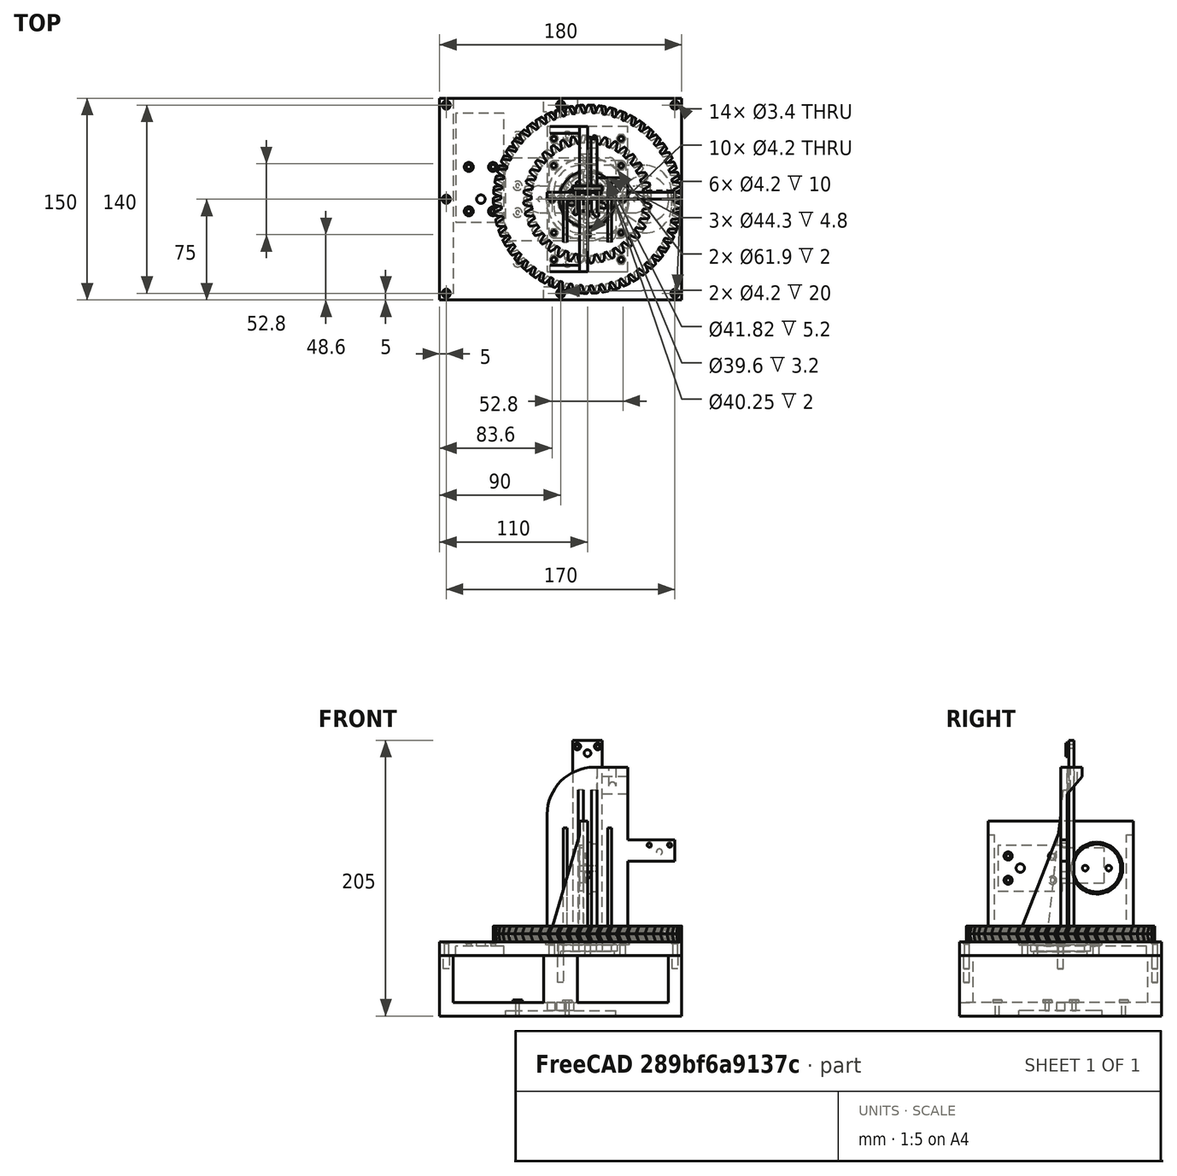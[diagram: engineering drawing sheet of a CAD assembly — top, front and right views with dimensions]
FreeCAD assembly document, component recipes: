
FREECAD ASSEMBLY — COMPONENT RECIPES ("antenna_tracker_alternative_gears_v0.6.5")

This assembly document has 24 components, labeled P0..P23 below (a component is one placed body or linked part). 18 of them carry a construction recipe — the FreeCAD feature program that regenerates the part from scratch, quoted from this document or its linked companion documents; the rest are supplied as boundary geometry only. No exploded tour is included for this assembly.
COMPONENT P0 — geometry summary ("GY_511_LSM303DLHC001"; no construction recipe available for this part):
  bounding box: 20.9 x 14.6 x 3.8 mm
  tessellated surface: 5,190 triangles
  volume: 500 mm^3 (43% of its bounding box)
COMPONENT P1 — geometry summary ("GY_511_LSM303DLHC002"; no construction recipe available for this part):
  bounding box: 20.9 x 14.6 x 3.8 mm
  tessellated surface: 5,190 triangles
  volume: 500 mm^3 (43% of its bounding box)
COMPONENT P2 — geometry summary ("GY_511_LSM303DLHC002"; no construction recipe available for this part):
  bounding box: 20.9 x 14.6 x 3.8 mm
  tessellated surface: 5,190 triangles
  volume: 500 mm^3 (43% of its bounding box)
COMPONENT P3 — geometry summary ("L298N v003"; no construction recipe available for this part):
  bounding box: 43.0 x 43.0 x 27.9 mm
  tessellated surface: 26,858 triangles
  volume: 10819 mm^3 (21% of its bounding box)
COMPONENT P4 — geometry summary ("ZWL-FP Motor_az"; no construction recipe available for this part):
  bounding box: 81.2 x 41.0 x 32.0 mm
  tessellated surface: 60,924 triangles
  volume: 36469 mm^3 (34% of its bounding box)
COMPONENT P5 — geometry summary ("ZWL-FP Motor_el"; no construction recipe available for this part):
  bounding box: 81.2 x 41.0 x 32.0 mm
  tessellated surface: 60,924 triangles
  volume: 36469 mm^3 (34% of its bounding box)
COMPONENT P6 — recipe-attached ("6707-2r_az", modeled in this document).
Construction recipe (the document's own serialized feature program — sketch geometry with constraints, then the solid features built on it; lengths are millimeters unless a unit is written):

FEATURE [Sketcher::SketchObject] Sketch002  label="bearing_outside"
  ArcFitTolerance = 1e-06
  AttachmentSupport = -> [XY_Plane004]
  ExternalTypes = [0]
  FullyConstrained = true
  MakeInternals = false
  MapMode = 5
  expr: Constraints[2] = VarSet.Base_bearing_outside_diameter
  expr: Constraints[3] = VarSet.Base_bearing_outside_diameter_inside
  sketch-geometry (2):
    g0: Circle CenterX=0 CenterY=0 CenterZ=0 NormalX=0 NormalY=0 NormalZ=1 AngleXU=0 Radius=22
    g1: Circle CenterX=0 CenterY=0 CenterZ=0 NormalX=0 NormalY=0 NormalZ=1 AngleXU=0 Radius=20.5
  constraints (4):
    c: Coincident(g0,g-1)
    c: Coincident(g1,g0)
    c: Diameter(g0) = 44
    c: Diameter(g1) = 41
FEATURE [PartDesign::Pad] Pad001
  Direction = (0,0,1)
  Length = 4.8
  Length2 = 10
  Profile = -> Sketch002
  ReferenceAxis = -> Sketch002 [N_Axis]
  Refine = true
  Suppressed = false
  Type = 0
  expr: Length = VarSet.Base_bearing_thickness
FEATURE [Sketcher::SketchObject] Sketch025  label="bearing_inside001"
  ArcFitTolerance = 1e-06
  AttachmentSupport = -> [XY_Plane004]
  ExternalTypes = [0]
  FullyConstrained = true
  MakeInternals = false
  MapMode = 5
  expr: Constraints[2] = VarSet.Base_bearing_inside_diameter_outside
  expr: Constraints[3] = VarSet.Base_bearing_inside_diameter
  sketch-geometry (5):
    g0: ArcOfCircle CenterX=0 CenterY=0 CenterZ=0 NormalX=0 NormalY=0 NormalZ=1 AngleXU=0 Radius=19 StartAngle=1.62345 EndAngle=7.80133
    g1: Circle CenterX=0 CenterY=0 CenterZ=0 NormalX=0 NormalY=0 NormalZ=1 AngleXU=0 Radius=17.5
    g2: LineSegment StartX=1 StartY=18.9737 StartZ=0 EndX=1 EndY=20.9737 EndZ=0
    g3: LineSegment StartX=-1 StartY=18.9737 StartZ=0 EndX=-1 EndY=20.9737 EndZ=0
    g4: LineSegment StartX=-1 StartY=20.9737 StartZ=0 EndX=1 EndY=20.9737 EndZ=0
  constraints (13):
    c: Coincident(g0,g-1)
    c: Coincident(g1,g0)
    c: Diameter(g0) = 38
    c: Diameter(g1) = 35
    c: Vertical(g2)
    c: Vertical(g3)
    c: Coincident(g4,g3)
    c: Coincident(g4,g2)
    c: Coincident(g0,g2)
    c: Coincident(g0,g3)
    c: DistanceX(g3,g2) = 2
    c: Symmetric(g3,g2,g-2)
    c: DistanceY(g0,g2) = 2
FEATURE [PartDesign::Pad] Pad024
  BaseFeature = -> Pad001
  Direction = (0,0,1)
  Length = 4.8
  Length2 = 10
  Profile = -> Sketch025
  ReferenceAxis = -> Sketch025 [N_Axis]
  Refine = true
  Suppressed = false
  Type = 0
  expr: Length = VarSet.Base_bearing_thickness
FEATURE [PartDesign::Body] Body002  label="6707-2r"
  AllowCompound = false
  Group = -> [Sketch002,Pad001,Sketch025,Pad024]
  Origin = -> Origin004
  Tip = -> Pad024
COMPONENT P7 — same part as P6; its construction recipe is shown at P6.
COMPONENT P8 — same part as P6; its construction recipe is shown at P6.
COMPONENT P9 — same part as P6; its construction recipe is shown at P6.
COMPONENT P10 — recipe-attached ("antenna_mount002", modeled in this document).
Construction recipe (the document's own serialized feature program — sketch geometry with constraints, then the solid features built on it; lengths are millimeters unless a unit is written):

FEATURE [Sketcher::SketchObject] Sketch031
  ArcFitTolerance = 1e-06
  AttachmentSupport = -> [XY_Plane022]
  ExternalTypes = [0]
  FullyConstrained = true
  MakeInternals = false
  MapMode = 5
  expr: Constraints[10] = VarSet.Base_antenna_base_x
  expr: Constraints[11] = VarSet.Base_antenna_base_y
  expr: Constraints[30] = VarSet.Base_antenna_base_x * 1.15
  expr: Constraints[31] = VarSet.Base_antenna_base_y * 1.15
  sketch-geometry (14):
    g0: LineSegment [constr] StartX=-25 StartY=25 StartZ=0 EndX=-25 EndY=-25 EndZ=0
    g1: LineSegment [constr] StartX=-25 StartY=-25 StartZ=0 EndX=25 EndY=-25 EndZ=0
    g2: LineSegment [constr] StartX=25 StartY=-25 StartZ=0 EndX=25 EndY=25 EndZ=0
    g3: LineSegment [constr] StartX=25 StartY=25 StartZ=0 EndX=-25 EndY=25 EndZ=0
    g4: GeomPoint [constr] X=0 Y=0 Z=0
    g5: Circle CenterX=-25 CenterY=25 CenterZ=0 NormalX=0 NormalY=0 NormalZ=1 AngleXU=0 Radius=1.55
    g6: Circle CenterX=25 CenterY=25 CenterZ=0 NormalX=0 NormalY=0 NormalZ=1 AngleXU=0 Radius=1.55
    g7: Circle CenterX=25 CenterY=-25 CenterZ=0 NormalX=0 NormalY=0 NormalZ=1 AngleXU=0 Radius=1.55
    g8: Circle CenterX=-25 CenterY=-25 CenterZ=0 NormalX=0 NormalY=0 NormalZ=1 AngleXU=0 Radius=1.55
    g9: LineSegment StartX=-28.75 StartY=28.75 StartZ=0 EndX=-28.75 EndY=-28.75 EndZ=0
    g10: LineSegment StartX=-28.75 StartY=-28.75 StartZ=0 EndX=28.75 EndY=-28.75 EndZ=0
    g11: LineSegment StartX=28.75 StartY=-28.75 StartZ=0 EndX=28.75 EndY=28.75 EndZ=0
    g12: LineSegment StartX=28.75 StartY=28.75 StartZ=0 EndX=-28.75 EndY=28.75 EndZ=0
    g13: GeomPoint [constr] X=0 Y=0 Z=0
  constraints (32):
    c: Coincident(g0,g1)
    c: Coincident(g1,g2)
    c: Coincident(g2,g3)
    c: Coincident(g3,g0)
    c: Vertical(g0)
    c: Vertical(g2)
    c: Horizontal(g1)
    c: Horizontal(g3)
    c: Symmetric(g2,g0,g4)
    c: Coincident(g4,g-1)
    c: DistanceX(g0,g2) = 50
    c: DistanceY(g0,g0) = 50
    c: Coincident(g5,g0)
    c: Coincident(g6,g2)
    c: Coincident(g7,g1)
    c: Coincident(g8,g0)
    c: Equal(g8,g7)
    c: Equal(g7,g6)
    c: Equal(g6,g5)
    c: Diameter(g5) = 3.1
    c: Coincident(g9,g10)
    c: Coincident(g10,g11)
    c: Coincident(g11,g12)
    c: Coincident(g12,g9)
    c: Vertical(g9)
    c: Vertical(g11)
    c: Horizontal(g10)
    c: Horizontal(g12)
    c: Symmetric(g11,g9,g13)
    c: Coincident(g13,g4)
    c: DistanceX(g12,g12) = 57.5
    c: DistanceY(g9,g9) = 57.5
FEATURE [PartDesign::Pad] Pad029
  Direction = (0,0,1)
  Length = 5
  Length2 = 10
  Profile = -> Sketch031
  ReferenceAxis = -> Sketch031 [N_Axis]
  Refine = true
  Suppressed = false
  Type = 0
FEATURE [Sketcher::SketchObject] Sketch059  label="vertical_base"
  ArcFitTolerance = 1e-06
  AttachmentSupport = -> [XY_Plane043]
  ExternalTypes = [0]
  FullyConstrained = true
  MakeInternals = false
  MapMode = 5
  sketch-geometry (4):
    g0: LineSegment StartX=-30 StartY=0 StartZ=0 EndX=30 EndY=0 EndZ=0
    g1: LineSegment StartX=30 StartY=0 StartZ=0 EndX=30 EndY=5 EndZ=0
    g2: LineSegment StartX=30 StartY=5 StartZ=0 EndX=-30 EndY=5 EndZ=0
    g3: LineSegment StartX=-30 StartY=5 StartZ=0 EndX=-30 EndY=0 EndZ=0
  constraints (11):
    c: Coincident(g0,g1)
    c: Coincident(g1,g2)
    c: Coincident(g2,g3)
    c: Coincident(g3,g0)
    c: Horizontal(g0)
    c: Vertical(g1)
    c: Vertical(g3)
    c: Distance(g1,g3) = 60
    c: Distance(g0,g2) = 5
    c: PointOnObject(g0,g-1)
    c: Symmetric(g2,g1,g-2)
FEATURE [PartDesign::Pad] Pad043
  Direction = (0,0,1)
  Length = 130
  Length2 = 10
  Profile = -> Sketch059
  ReferenceAxis = -> Sketch059 [N_Axis]
  Refine = true
  Suppressed = false
  Type = 0
FEATURE [Sketcher::SketchObject] Sketch060  label="trust"
  ArcFitTolerance = 1e-06
  AttachmentOffset = pos=(0,0,-18) rot=(0,0,1;0rad)
  AttachmentSupport = -> [YZ_Plane043]
  ExternalTypes = [0]
  FullyConstrained = true
  MakeInternals = false
  MapMode = 5
  Placement = pos=(-18,0,0) rot=(0.57735,0.57735,0.57735;2.0944rad)
  sketch-geometry (4):
    g0: LineSegment StartX=0 StartY=0 StartZ=0 EndX=0 EndY=85 EndZ=0
    g1: LineSegment StartX=-32 StartY=0 StartZ=0 EndX=0 EndY=0 EndZ=0
    g2: LineSegment StartX=-32 StartY=0 StartZ=0 EndX=-32 EndY=3 EndZ=0
    g3: LineSegment StartX=-32 StartY=3 StartZ=0 EndX=0 EndY=85 EndZ=0
  constraints (11):
    c: Coincident(g-1,g0)
    c: PointOnObject(g0,g-2)
    c: PointOnObject(g1,g-1)
    c: Coincident(g1,g0)
    c: DistanceY(g-1,g0) = 85
    c: DistanceX(g1,g0) = 32
    c: Coincident(g2,g3)
    c: Coincident(g3,g0)
    c: Parallel(g2,g0)
    c: Distance(g2,g2) = 3
    c: Coincident(g2,g1)
FEATURE [PartDesign::Pad] Pad044
  BaseFeature = -> Pad043
  Direction = (1,0,0)
  Length = 3
  Length2 = 10
  Profile = -> Sketch060
  ReferenceAxis = -> Sketch060 [N_Axis]
  Refine = true
  Suppressed = false
  Type = 0
FEATURE [PartDesign::Mirrored] Mirrored
  BaseFeature = -> Pad044
  MirrorPlane = -> YZ_Plane043
  Originals = -> [Pad044]
  Refine = true
  Suppressed = false
  TransformMode = 0
FEATURE [Sketcher::SketchObject] Sketch061  label="antenna_hole"
  ArcFitTolerance = 1e-06
  AttachmentSupport = -> [Mirrored]
  ExternalTypes = [0]
  FullyConstrained = true
  MakeInternals = false
  MapMode = 5
  Placement = pos=(0,5,0) rot=(0,0.707107,0.707107;3.14159rad)
  sketch-geometry (1):
    g0: Circle CenterX=0 CenterY=50 CenterZ=0 NormalX=0 NormalY=0 NormalZ=1 AngleXU=0 Radius=2.6
  constraints (3):
    c: PointOnObject(g0,g-2)
    c: DistanceY(g-1,g0) = 50
    c: Diameter(g0) = 5.2
FEATURE [Sketcher::SketchObject] Sketch062  label="vertical_mount_antenna"
  ArcFitTolerance = 1e-06
  ExternalTypes = [0]
  FullyConstrained = true
  MakeInternals = false
  MapMode = 5
  Placement = pos=(0,0,130) rot=(0,0,1;0rad)
  sketch-geometry (6):
    g0: LineSegment StartX=7 StartY=0 StartZ=0 EndX=30 EndY=0 EndZ=0
    g1: LineSegment StartX=30 StartY=0 StartZ=0 EndX=30 EndY=16 EndZ=0
    g2: LineSegment StartX=30 StartY=16 StartZ=0 EndX=7 EndY=16 EndZ=0
    g3: LineSegment StartX=7 StartY=16 StartZ=0 EndX=7 EndY=0 EndZ=0
    g4: Circle CenterX=18.5 CenterY=10 CenterZ=0 NormalX=0 NormalY=0 NormalZ=1 AngleXU=0 Radius=2.6
    g5: LineSegment [constr] StartX=18.5 StartY=0 StartZ=0 EndX=18.5 EndY=16 EndZ=0
  constraints (17):
    c: Coincident(g0,g1)
    c: Coincident(g1,g2)
    c: Coincident(g2,g3)
    c: Coincident(g3,g0)
    c: Horizontal(g2)
    c: Vertical(g1)
    c: Vertical(g3)
    c: Distance(g1,g3) = 23
    c: Distance(g0,g2) = 16
    c: PointOnObject(g0,g-1)
    c: Diameter(g4) = 5.2
    c: DistanceY(g-1,g4) = 10
    c: Symmetric(g0,g0,g5)
    c: Symmetric(g2,g2,g5)
    c: PointOnObject(g0,g-1)
    c: PointOnObject(g4,g5)
    c: DistanceX(g-1,g0) = 7
FEATURE [PartDesign::Pad] Pad045
  BaseFeature = -> Mirrored
  Direction = (0,0,1)
  Length = 20
  Length2 = 10
  Profile = -> Sketch062
  ReferenceAxis = -> Sketch062 [N_Axis]
  Refine = true
  Reversed = true
  Suppressed = false
  Type = 0
FEATURE [Sketcher::SketchObject] Sketch063
  ArcFitTolerance = 1e-06
  AttachmentSupport = -> [YZ_Plane043]
  ExternalGeometry = -> [Pad045]
  ExternalTypes = [0,0,0]
  FullyConstrained = true
  MakeInternals = false
  MapMode = 5
  Placement = pos=(0,0,0) rot=(0.57735,0.57735,0.57735;2.0944rad)
  sketch-geometry (3):
    g0: LineSegment StartX=16 StartY=110 StartZ=0 EndX=16 EndY=123 EndZ=0
    g1: LineSegment StartX=16 StartY=123 StartZ=0 EndX=5 EndY=110 EndZ=0
    g2: LineSegment StartX=5 StartY=110 StartZ=0 EndX=16 EndY=110 EndZ=0
  constraints (8):
    c: Coincident(g0,g1)
    c: PointOnObject(g0,g-4)
    c: Coincident(g2,g1)
    c: Coincident(g2,g0)
    c: Coincident(g0,g-4)
    c: Coincident(g1,g-5)
    c: Angle(g1,g0) = 0.702257
    c: DistanceY(g0,g-4) = 7
FEATURE [PartDesign::Pocket] Pocket041
  BaseFeature = -> Pad045
  Direction = (-1,0,0)
  Length = 5
  Length2 = 5
  Midplane = true
  Profile = -> Sketch063
  ReferenceAxis = -> Sketch063 [N_Axis]
  Refine = true
  Suppressed = false
  Type = 1
FEATURE [PartDesign::Fillet] Fillet001
  Base = -> Pad029 [Edge5,Edge8,Edge1,Edge2]
  BaseFeature = -> Pad029
  Radius = 4
  Refine = true
  SupportTransform = false
  Suppressed = false
  UseAllEdges = false
FEATURE [PartDesign::Body] Body011  label="antenna_mount_body"
  AllowCompound = false
  Group = -> [Sketch031,Pad029,Fillet001]
  Origin = -> Origin038
  Tip = -> Fillet001
FEATURE [Sketcher::SketchObject] Sketch067  label="sensor_mount"
  ArcFitTolerance = 1e-06
  AttachmentSupport = -> [XZ_Plane043]
  ExternalTypes = [0]
  FullyConstrained = true
  MakeInternals = false
  MapMode = 5
  Placement = pos=(0,0,0) rot=(1,0,0;1.5708rad)
  sketch-geometry (12):
    g0: LineSegment StartX=0 StartY=76 StartZ=0 EndX=0 EndY=60 EndZ=0
    g1: LineSegment StartX=0 StartY=60 StartZ=0 EndX=65 EndY=60 EndZ=0
    g2: LineSegment StartX=65 StartY=60 StartZ=0 EndX=65 EndY=76 EndZ=0
    g3: LineSegment StartX=65 StartY=76 StartZ=0 EndX=0 EndY=76 EndZ=0
    g4: LineSegment [constr] StartX=65 StartY=72 StartZ=0 EndX=0 EndY=72 EndZ=0
    g5: Circle CenterX=61 CenterY=72 CenterZ=0 NormalX=0 NormalY=0 NormalZ=1 AngleXU=0 Radius=1.4
    g6: Circle CenterX=45.9 CenterY=72 CenterZ=0 NormalX=0 NormalY=0 NormalZ=1 AngleXU=0 Radius=1.4
    g7: Circle CenterX=45.9 CenterY=72 CenterZ=0 NormalX=0 NormalY=0 NormalZ=1 AngleXU=0 Radius=2.2
    g8: Circle CenterX=61 CenterY=72 CenterZ=0 NormalX=0 NormalY=0 NormalZ=1 AngleXU=0 Radius=2.2
    g9: Circle CenterX=53.45 CenterY=67 CenterZ=0 NormalX=0 NormalY=0 NormalZ=1 AngleXU=0 Radius=2.2
    g10: GeomPoint X=53.45 Y=72 Z=0
    g11: LineSegment [constr] StartX=53.45 StartY=72 StartZ=0 EndX=53.45 EndY=67 EndZ=0
  constraints (32):
    c: Coincident(g0,g1)
    c: Coincident(g1,g2)
    c: Coincident(g2,g3)
    c: Coincident(g3,g0)
    c: Vertical(g0)
    c: Vertical(g2)
    c: Horizontal(g1)
    c: Horizontal(g3)
    c: PointOnObject(g0,g-2)
    c: DistanceY(g0,g0) = 16
    c: DistanceX(g0,g1) = 65
    c: DistanceY(g-1,g0) = 60
    c: PointOnObject(g4,g2)
    c: PointOnObject(g4,g0)
    c: Horizontal(g4)
    c: Distance(g4,g2) = 4
    c: PointOnObject(g5,g4)
    c: PointOnObject(g6,g4)
    c: Diameter(g6) = 2.8
    c: Coincident(g7,g6)
    c: Coincident(g8,g5)
    c: Equal(g6,g5)
    c: Diameter(g7) = 4.4
    c: Equal(g7,g8)
    c: DistanceX(g6,g5) = 15.1
    c: DistanceX(g5,g4) = 4
    c: Equal(g7,g9)
    c: Symmetric(g6,g5,g10)
    c: Coincident(g11,g10)
    c: Vertical(g11)
    c: Coincident(g9,g11)
    c: DistanceY(g9,g10) = 5
FEATURE [PartDesign::Pad] Pad048
  BaseFeature = -> Pocket041
  Direction = (0,-1,2e-16)
  Length = 5
  Length2 = 10
  Profile = -> Sketch067 [Edge2,Edge1,Edge4,Edge3]
  ReferenceAxis = -> Sketch067 [N_Axis]
  Refine = true
  Reversed = true
  Suppressed = false
  Type = 0
FEATURE [PartDesign::Pad] Pad049
  BaseFeature = -> Pad048
  Direction = (0,-1,2e-16)
  Length = 6
  Length2 = 10
  Profile = -> Sketch067 [Edge8,Edge9,Edge7]
  ReferenceAxis = -> Sketch067 [N_Axis]
  Refine = true
  Reversed = true
  Suppressed = false
  Type = 0
FEATURE [PartDesign::Pocket] Pocket044
  BaseFeature = -> Pad049
  Direction = (0,1,-2e-16)
  Length = 5
  Length2 = 5
  Midplane = true
  Profile = -> Sketch067 [Edge6,Edge5]
  ReferenceAxis = -> Sketch067 [N_Axis]
  Refine = true
  Suppressed = false
  Type = 1
FEATURE [PartDesign::Pocket] Pocket045
  BaseFeature = -> Pocket044
  Direction = (0,-1,2e-16)
  Length = 5
  Length2 = 5
  Midplane = true
  Profile = -> Sketch061
  ReferenceAxis = -> Sketch061 [N_Axis]
  Refine = true
  Suppressed = false
  Type = 1
FEATURE [PartDesign::Fillet] Fillet
  Base = -> Pocket045 [Edge30]
  BaseFeature = -> Pocket045
  Radius = 35
  Refine = true
  SupportTransform = false
  Suppressed = false
  UseAllEdges = false
FEATURE [PartDesign::Body] Body019  label="helix_yagi"
  AllowCompound = false
  Group = -> [Sketch059,Pad043,Sketch060,Pad044,Mirrored,Sketch061,Sketch062,Pad045,Sketch063,Pocket041,Sketch067,Pad048,Pad049,Pocket044,Pocket045,Fillet]
  Origin = -> Origin080
  Tip = -> Fillet
COMPONENT P11 — recipe-attached ("base003", modeled in this document).
Construction recipe (the document's own serialized feature program — sketch geometry with constraints, then the solid features built on it; lengths are millimeters unless a unit is written):

FEATURE [Sketcher::SketchObject] Sketch001  label="outside"
  ArcFitTolerance = 1e-06
  AttachmentSupport = -> [XY_Plane003]
  ExternalTypes = [0]
  FullyConstrained = true
  MakeInternals = false
  MapMode = 5
  expr: Constraints[8] = VarSet.Base_base_y
  expr: Constraints[9] = VarSet.Base_base_x
  sketch-geometry (5):
    g0: LineSegment StartX=-110 StartY=-75 StartZ=0 EndX=70 EndY=-75 EndZ=0
    g1: LineSegment StartX=70 StartY=-75 StartZ=0 EndX=70 EndY=75 EndZ=0
    g2: LineSegment StartX=70 StartY=75 StartZ=0 EndX=-110 EndY=75 EndZ=0
    g3: LineSegment StartX=-110 StartY=75 StartZ=0 EndX=-110 EndY=-75 EndZ=0
    g4: GeomPoint [constr] X=0 Y=0 Z=0
  constraints (12):
    c: Coincident(g0,g1)
    c: Coincident(g1,g2)
    c: Coincident(g2,g3)
    c: Coincident(g3,g0)
    c: Horizontal(g0)
    c: Horizontal(g2)
    c: Vertical(g1)
    c: Coincident(g4,g-1)
    c: DistanceY(g0,g2) = 150
    c: DistanceX(g2,g1) = 180
    c: DistanceX(g2,g-1) = 110
    c: Symmetric(g0,g2,g-1)
FEATURE [PartDesign::Pad] Pad
  Direction = (0,0,1)
  Length = 10
  Length2 = 10
  Profile = -> Sketch001
  ReferenceAxis = -> Sketch001 [N_Axis]
  Refine = true
  Reversed = true
  Suppressed = false
  Type = 0
  expr: Length = VarSet.Base_base_thickness
FEATURE [Sketcher::SketchObject] Sketch  label="motor"
  ArcFitTolerance = 1e-06
  AttachmentSupport = -> [XY_Plane003]
  ExternalTypes = [0]
  FullyConstrained = true
  MakeInternals = false
  MapMode = 5
  expr: Constraints[0] = 6 mm + VarSet.Base_tolerance_inside_circle
  expr: Constraints[2] = VarSet.Base_distance_grat_az
  sketch-geometry (10):
    g0: Circle CenterX=-79.3 CenterY=0 CenterZ=0 NormalX=0 NormalY=0 NormalZ=1 AngleXU=0 Radius=3.15
    g1: LineSegment [constr] StartX=-88.3 StartY=-9 StartZ=0 EndX=-70.3 EndY=-9 EndZ=0
    g2: Circle CenterX=-88.3 CenterY=-9 CenterZ=0 NormalX=0 NormalY=0 NormalZ=1 AngleXU=0 Radius=1.5
    g3: Circle CenterX=-70.3 CenterY=-9 CenterZ=0 NormalX=0 NormalY=0 NormalZ=1 AngleXU=0 Radius=1.5
    g4: Circle CenterX=-88.3 CenterY=24 CenterZ=0 NormalX=0 NormalY=0 NormalZ=1 AngleXU=0 Radius=1.5
    g5: LineSegment [constr] StartX=-70.3 StartY=-9 StartZ=0 EndX=-70.3 EndY=24 EndZ=0
    g6: LineSegment [constr] StartX=-70.3 StartY=24 StartZ=0 EndX=-88.3 EndY=24 EndZ=0
    g7: Circle CenterX=-70.3 CenterY=24 CenterZ=0 NormalX=0 NormalY=0 NormalZ=1 AngleXU=0 Radius=1.5
    g8: LineSegment [constr] StartX=-88.3 StartY=24 StartZ=0 EndX=-88.3 EndY=-9 EndZ=0
    g9: LineSegment [constr] StartX=-79.3 StartY=24 StartZ=0 EndX=-79.3 EndY=-9 EndZ=0
  constraints (26):
    c: Diameter(g0) = 6.3
    c: PointOnObject(g0,g-1)
    c: DistanceX(g0,g-1) = 79.3
    c: Coincident(g1,g5)
    c: Coincident(g5,g6)
    c: Coincident(g2,g1)
    c: Coincident(g4,g6)
    c: Coincident(g7,g5)
    c: Coincident(g3,g1)
    c: Equal(g2,g4)
    c: Equal(g4,g7)
    c: Equal(g7,g3)
    c: Diameter(g2) = 3
    c: Coincident(g8,g4)
    c: Coincident(g8,g1)
    c: Vertical(g8)
    c: DistanceX(g1,g1) = 18
    c: DistanceY(g1,g5) = 33
    c: Perpendicular(g1,g8)
    c: Perpendicular(g5,g6)
    c: Perpendicular(g6,g8)
    c: Symmetric(g6,g6,g9)
    c: Vertical(g9)
    c: PointOnObject(g9,g1)
    c: PointOnObject(g0,g9)
    c: DistanceY(g9,g0) = 9
FEATURE [PartDesign::Pocket] Pocket009
  BaseFeature = -> Pad
  Direction = (0,0,-1)
  Length = 5
  Length2 = 5
  Midplane = true
  Profile = -> Sketch [Edge1]
  ReferenceAxis = -> Sketch [N_Axis]
  Refine = true
  Suppressed = false
  Type = 1
FEATURE [Sketcher::SketchObject] Sketch019  label="motor_resess"
  ArcFitTolerance = 1e-06
  AttachmentOffset = pos=(0,0,-10) rot=(0,0,1;0rad)
  AttachmentSupport = -> [XY_Plane003]
  ExternalTypes = [0]
  FullyConstrained = true
  MakeInternals = false
  MapMode = 5
  Placement = pos=(0,0,-10) rot=(0,0,1;0rad)
  expr: .AttachmentOffset.Base.z = -1 * VarSet.Base_base_thickness
  sketch-geometry (4):
    g0: LineSegment StartX=-98 StartY=64 StartZ=0 EndX=-98 EndY=-17 EndZ=0
    g1: LineSegment StartX=-98 StartY=-17 StartZ=0 EndX=-62 EndY=-17 EndZ=0
    g2: LineSegment StartX=-62 StartY=-17 StartZ=0 EndX=-62 EndY=64 EndZ=0
    g3: LineSegment StartX=-62 StartY=64 StartZ=0 EndX=-98 EndY=64 EndZ=0
  constraints (12):
    c: Coincident(g0,g1)
    c: Coincident(g1,g2)
    c: Coincident(g2,g3)
    c: Coincident(g3,g0)
    c: Vertical(g2)
    c: Horizontal(g1)
    c: Horizontal(g3)
    c: DistanceY(g0,g0) = 81
    c: DistanceX(g0,g2) = 36
    c: DistanceX(g2,g-1) = 62
    c: DistanceY(g-1,g2) = 64
    c: Perpendicular(g1,g0)
FEATURE [PartDesign::Pocket] Pocket010  label="motor_resess001"
  BaseFeature = -> Pocket009
  Direction = (0,0,-1)
  Length = 7
  Length2 = 5
  Profile = -> Sketch019
  ReferenceAxis = -> Sketch019 [N_Axis]
  Refine = true
  Reversed = true
  Suppressed = false
  Type = 0
FEATURE [Sketcher::SketchObject] Sketch023  label="central_hole"
  ArcFitTolerance = 1e-06
  AttachmentSupport = -> [XY_Plane003]
  ExternalTypes = [0]
  FullyConstrained = true
  MakeInternals = false
  MapMode = 5
  expr: Constraints[2] = VarSet.Base_bearing_outside_diameter_with_tolerance
  expr: Constraints[3] = VarSet.Base_bearing_cap_outside_diameter + VarSet.Base_tolerance_inside_circle
  expr: Constraints[5] = VarSet.Base_bearing_outside_diameter * 0.9
  sketch-geometry (3):
    g0: Circle CenterX=0 CenterY=0 CenterZ=0 NormalX=0 NormalY=0 NormalZ=1 AngleXU=0 Radius=30.95
    g1: Circle CenterX=0 CenterY=0 CenterZ=0 NormalX=0 NormalY=0 NormalZ=1 AngleXU=0 Radius=22.15
    g2: Circle CenterX=0 CenterY=0 CenterZ=0 NormalX=0 NormalY=0 NormalZ=1 AngleXU=0 Radius=19.8
  constraints (6):
    c: Coincident(g0,g-1)
    c: Coincident(g1,g0)
    c: Diameter(g1) = 44.3
    c: Diameter(g0) = 61.9
    c: Coincident(g2,g0)
    c: Diameter(g2) = 39.6
FEATURE [PartDesign::Pocket] Pocket014
  BaseFeature = -> Pocket010
  Direction = (0,0,-1)
  Length = 6.8
  Length2 = 5
  Profile = -> Sketch023 [Edge2]
  ReferenceAxis = -> Sketch023 [N_Axis]
  Refine = true
  Suppressed = false
  Type = 0
  expr: Length = VarSet.Base_bearing_thickness + VarSet.Base_base_bearing_cap_thickness
FEATURE [PartDesign::Pocket] Pocket015
  BaseFeature = -> Pocket014
  Direction = (0,0,-1)
  Length = 2
  Length2 = 5
  Profile = -> Sketch023 [Edge1]
  ReferenceAxis = -> Sketch023 [N_Axis]
  Refine = true
  Suppressed = false
  Type = 0
  expr: Length = VarSet.Base_base_bearing_cap_thickness
FEATURE [Sketcher::SketchObject] Sketch024  label="hole_for_bearing_cap_outside"
  ArcFitTolerance = 1e-06
  AttachmentSupport = -> [XY_Plane003]
  ExternalTypes = [0]
  FullyConstrained = true
  MakeInternals = false
  MapMode = 5
  expr: Constraints[1] = VarSet.Base_m3_insert
  expr: Constraints[2] = VarSet.Base_bearing_cap_outside_diameter_hole
  sketch-geometry (1):
    g0: Circle CenterX=0 CenterY=26.4 CenterZ=0 NormalX=0 NormalY=0 NormalZ=1 AngleXU=0 Radius=2.1
  constraints (3):
    c: PointOnObject(g0,g-2)
    c: Diameter(g0) = 4.2
    c: DistanceY(g-1,g0) = 26.4
FEATURE [PartDesign::Pocket] Pocket016
  BaseFeature = -> Pocket015
  Direction = (0,0,-1)
  Length = 5
  Length2 = 5
  Profile = -> Sketch024
  ReferenceAxis = -> Sketch024 [N_Axis]
  Refine = true
  Suppressed = false
  Type = 1
FEATURE [PartDesign::PolarPattern] PolarPattern
  Angle = 360
  Axis = -> Sketch024 [N_Axis]
  BaseFeature = -> Pocket016
  Mode = 0
  Occurrences = 4
  Offset = 120
  Originals = -> [Pocket016]
  Refine = true
  Suppressed = false
  TransformMode = 0
FEATURE [PartDesign::Pocket] Pocket017
  BaseFeature = -> PolarPattern
  Direction = (0,0,-1)
  Length = 5
  Length2 = 5
  Profile = -> Sketch023 [Edge3]
  ReferenceAxis = -> Sketch023 [N_Axis]
  Refine = true
  Suppressed = false
  Type = 1
FEATURE [Sketcher::SketchObject] Sketch035  label="base_hole_for_connection_with_onother"
  ArcFitTolerance = 1e-06
  AttachmentSupport = -> [XY_Plane003]
  ExternalTypes = [1,1]
  FullyConstrained = true
  MakeInternals = false
  MapMode = 5
  expr: Constraints[14] = 3.3 mm
  expr: Constraints[28] = VarSet.Base_base_y
  expr: Constraints[29] = VarSet.Base_base_x
  expr: Constraints[30] = VarSet.Base_base_x_small
  sketch-geometry (16):
    g0: LineSegment [constr] StartX=-105 StartY=70 StartZ=0 EndX=-105 EndY=-70 EndZ=0
    g1: LineSegment [constr] StartX=-105 StartY=-70 StartZ=0 EndX=65 EndY=-70 EndZ=0
    g2: LineSegment [constr] StartX=65 StartY=-70 StartZ=0 EndX=65 EndY=70 EndZ=0
    g3: LineSegment [constr] StartX=65 StartY=70 StartZ=0 EndX=-105 EndY=70 EndZ=0
    g4: Circle CenterX=-105 CenterY=70 CenterZ=0 NormalX=0 NormalY=0 NormalZ=1 AngleXU=0 Radius=1.65
    g5: Circle CenterX=65 CenterY=70 CenterZ=0 NormalX=0 NormalY=0 NormalZ=1 AngleXU=0 Radius=1.65
    g6: Circle CenterX=65 CenterY=-70 CenterZ=0 NormalX=0 NormalY=0 NormalZ=1 AngleXU=0 Radius=1.65
    g7: Circle CenterX=-105 CenterY=-70 CenterZ=0 NormalX=0 NormalY=0 NormalZ=1 AngleXU=0 Radius=1.65
    g8: Circle CenterX=-20 CenterY=70 CenterZ=0 NormalX=0 NormalY=0 NormalZ=1 AngleXU=0 Radius=1.65
    g9: Circle CenterX=65 CenterY=0 CenterZ=0 NormalX=0 NormalY=0 NormalZ=1 AngleXU=0 Radius=1.65
    g10: Circle CenterX=-20 CenterY=-70 CenterZ=0 NormalX=0 NormalY=0 NormalZ=1 AngleXU=0 Radius=1.65
    g11: Circle CenterX=-105 CenterY=-6.3e-15 CenterZ=0 NormalX=0 NormalY=0 NormalZ=1 AngleXU=0 Radius=1.65
    g12: LineSegment [constr] StartX=-110 StartY=75 StartZ=0 EndX=-110 EndY=-75 EndZ=0
    g13: LineSegment [constr] StartX=-110 StartY=-75 StartZ=0 EndX=70 EndY=-75 EndZ=0
    g14: LineSegment [constr] StartX=70 StartY=-75 StartZ=0 EndX=70 EndY=75 EndZ=0
    g15: LineSegment [constr] StartX=70 StartY=75 StartZ=0 EndX=-110 EndY=75 EndZ=0
  constraints (39):
    c: Coincident(g0,g1)
    c: Coincident(g1,g2)
    c: Coincident(g2,g3)
    c: Coincident(g3,g0)
    c: Vertical(g2)
    c: Horizontal(g1)
    c: Horizontal(g3)
    c: Coincident(g4,g0)
    c: Coincident(g5,g2)
    c: Coincident(g6,g1)
    c: Coincident(g7,g0)
    c: Equal(g7,g6)
    c: Equal(g6,g5)
    c: Equal(g5,g4)
    c: Diameter(g4) = 3.3
    c: Symmetric(g0,g0,g11)
    c: Equal(g11,g10)
    c: Equal(g10,g8)
    c: Equal(g8,g9)
    c: Equal(g9,g4)
    c: Coincident(g12,g13)
    c: Coincident(g13,g14)
    c: Coincident(g14,g15)
    c: Coincident(g15,g12)
    c: Vertical(g14)
    c: Horizontal(g13)
    c: Horizontal(g15)
    c: Symmetric(g12,g12,g-1)
    c: DistanceY(g12,g12) = 150
    c: DistanceX(g12,g14) = 180
    c: DistanceX(g12,g-1) = 110
    c: DistanceX(g12,g0) = 5
    c: Distance(g2,g14) = 5
    c: Symmetric(g0,g0,g-1)
    c: DistanceY(g0,g12) = 5
    c: Symmetric(g0,g1,g10)
    c: Symmetric(g0,g2,g8)
    c: PointOnObject(g9,g-1)
    c: PointOnObject(g9,g2)
FEATURE [Part::DatumPlane] Plane001
  AttachmentOffset = pos=(0,0,-10) rot=(0,0,1;0rad)
  AttachmentSupport = -> [Origin040]
  MapMode = 5
  Placement = pos=(0,0,-10) rot=(0,0,1;0rad)
  expr: .AttachmentOffset.Base.z = -1 * VarSet.Base_base_thickness
FEATURE [Sketcher::SketchObject] Sketch036
  ArcFitTolerance = 1e-06
  AttachmentSupport = -> [Plane001]
  ExternalTypes = [0]
  FullyConstrained = true
  MakeInternals = false
  MapMode = 5
  Placement = pos=(0,0,-10) rot=(0,0,1;0rad)
  expr: Constraints[10] = VarSet.Base_base_x
  expr: Constraints[11] = VarSet.Base_base_y
  sketch-geometry (5):
    g0: LineSegment StartX=-90 StartY=75 StartZ=0 EndX=-90 EndY=-75 EndZ=0
    g1: LineSegment StartX=-90 StartY=-75 StartZ=0 EndX=90 EndY=-75 EndZ=0
    g2: LineSegment StartX=90 StartY=-75 StartZ=0 EndX=90 EndY=75 EndZ=0
    g3: LineSegment StartX=90 StartY=75 StartZ=0 EndX=-90 EndY=75 EndZ=0
    g4: GeomPoint [constr] X=0 Y=0 Z=0
  constraints (12):
    c: Coincident(g0,g1)
    c: Coincident(g1,g2)
    c: Coincident(g2,g3)
    c: Coincident(g3,g0)
    c: Vertical(g0)
    c: Vertical(g2)
    c: Horizontal(g1)
    c: Horizontal(g3)
    c: Symmetric(g2,g0,g4)
    c: Coincident(g4,g-1)
    c: DistanceX(g0,g2) = 180
    c: DistanceY(g0,g0) = 150
FEATURE [PartDesign::Pad] Pad032
  Direction = (0,0,1)
  Length = 40
  Length2 = 10
  Placement = pos=(0,0,-10) rot=(0,0,1;0rad)
  Profile = -> Sketch036
  ReferenceAxis = -> Sketch036 [N_Axis]
  Refine = true
  Reversed = true
  Suppressed = false
  Type = 0
FEATURE [PartDesign::Thickness] Thickness
  Base = -> Pad032 [Face5]
  BaseFeature = -> Pad032
  Intersection = false
  Join = 0
  Mode = 0
  Refine = true
  Reversed = true
  SupportTransform = false
  Suppressed = false
  Value = 8
FEATURE [Sketcher::SketchObject] Sketch037
  ArcFitTolerance = 1e-06
  AttachmentSupport = -> [Plane001]
  ExternalTypes = [0]
  FullyConstrained = true
  MakeInternals = false
  MapMode = 5
  Placement = pos=(0,0,-10) rot=(0,0,1;0rad)
  expr: Constraints[25] = VarSet.Base_m3_insert
  expr: Constraints[26] = VarSet.Base_base_x - 2 * 5 mm
  expr: Constraints[27] = VarSet.Base_base_y - 2 * 5 mm
  sketch-geometry (13):
    g0: LineSegment [constr] StartX=-85 StartY=70 StartZ=0 EndX=-85 EndY=-70 EndZ=0
    g1: LineSegment [constr] StartX=-85 StartY=-70 StartZ=0 EndX=85 EndY=-70 EndZ=0
    g2: LineSegment [constr] StartX=85 StartY=-70 StartZ=0 EndX=85 EndY=70 EndZ=0
    g3: LineSegment [constr] StartX=85 StartY=70 StartZ=0 EndX=-85 EndY=70 EndZ=0
    g4: GeomPoint [constr] X=-2e-16 Y=0 Z=0
    g5: Circle CenterX=-85 CenterY=70 CenterZ=0 NormalX=0 NormalY=0 NormalZ=1 AngleXU=0 Radius=2.1
    g6: Circle CenterX=-1e-16 CenterY=70 CenterZ=0 NormalX=0 NormalY=0 NormalZ=1 AngleXU=0 Radius=2.1
    g7: Circle CenterX=85 CenterY=70 CenterZ=0 NormalX=0 NormalY=0 NormalZ=1 AngleXU=0 Radius=2.1
    g8: Circle CenterX=85 CenterY=1e-16 CenterZ=0 NormalX=0 NormalY=0 NormalZ=1 AngleXU=0 Radius=2.1
    g9: Circle CenterX=85 CenterY=-70 CenterZ=0 NormalX=0 NormalY=0 NormalZ=1 AngleXU=0 Radius=2.1
    g10: Circle CenterX=-1e-16 CenterY=-70 CenterZ=0 NormalX=0 NormalY=0 NormalZ=1 AngleXU=0 Radius=2.1
    g11: Circle CenterX=-85 CenterY=-70 CenterZ=0 NormalX=0 NormalY=0 NormalZ=1 AngleXU=0 Radius=2.1
    g12: Circle CenterX=-85 CenterY=1e-16 CenterZ=0 NormalX=0 NormalY=0 NormalZ=1 AngleXU=0 Radius=2.1
  constraints (28):
    c: Coincident(g0,g1)
    c: Coincident(g1,g2)
    c: Coincident(g2,g3)
    c: Coincident(g3,g0)
    c: Vertical(g0)
    c: Vertical(g2)
    c: Horizontal(g1)
    c: Horizontal(g3)
    c: Symmetric(g2,g0,g4)
    c: Coincident(g4,g-1)
    c: Coincident(g5,g0)
    c: Symmetric(g3,g3,g6)
    c: Coincident(g7,g2)
    c: Symmetric(g2,g2,g8)
    c: Coincident(g9,g1)
    c: Symmetric(g1,g1,g10)
    c: Coincident(g11,g0)
    c: Symmetric(g0,g0,g12)
    c: Equal(g11,g10)
    c: Equal(g10,g9)
    c: Equal(g9,g8)
    c: Equal(g8,g7)
    c: Equal(g7,g6)
    c: Equal(g6,g12)
    c: Equal(g12,g5)
    c: Diameter(g5) = 4.2
    c: DistanceX(g0,g2) = 170
    c: DistanceY(g0,g0) = 140
FEATURE [PartDesign::Body] Body012  label="base_mount_down"
  AllowCompound = false
  Group = -> [Sketch036,Pad032,Plane001,Thickness,Sketch037]
  Origin = -> Origin040
  Tip = -> Thickness
FEATURE [PartDesign::Hole] Hole005
  BaseFeature = -> Pocket017
  CustomThreadClearance = 0
  Depth = 25
  DepthType = 0
  Diameter = 3.4
  DrillForDepth = false
  DrillPoint = 1
  DrillPointAngle = 118
  HoleCutCountersinkAngle = 90
  HoleCutCustomValues = false
  HoleCutDepth = 0
  HoleCutDiameter = 6.1
  HoleCutType = 2
  ModelThread = false
  Profile = -> Sketch035
  Refine = true
  Suppressed = false
  Tapered = false
  TaperedAngle = 90
  ThreadClass = 0
  ThreadDepth = 25
  ThreadDepthType = 0
  ThreadDiameter = 3
  ThreadDirection = 0
  ThreadFit = 0
  ThreadSize = 9
  ThreadType = 1
  Threaded = false
  UseCustomThreadClearance = false
FEATURE [Part::DatumPlane] Plane002
  AttachmentOffset = pos=(0,0,-10) rot=(0,0,1;0rad)
  AttachmentSupport = -> [Origin042]
  MapMode = 5
  Placement = pos=(0,0,-10) rot=(0,0,1;0rad)
  expr: .AttachmentOffset.Base.z = -1 * VarSet.Base_base_thickness
FEATURE [Sketcher::SketchObject] Sketch039  label="base004"
  ArcFitTolerance = 1e-06
  AttachmentSupport = -> [XZ_Plane024]
  ExternalTypes = [0]
  FullyConstrained = true
  MakeInternals = false
  MapMode = 5
  Placement = pos=(0,0,0) rot=(1,0,0;1.5708rad)
  expr: Constraints[24] = VarSet.Base_base_x
  expr: Constraints[25] = VarSet.Base_base_thickness
  expr: Constraints[27] = VarSet.Base_base_x_small
  sketch-geometry (10):
    g0: LineSegment StartX=-110 StartY=-10 StartZ=0 EndX=-100 EndY=-10 EndZ=0
    g1: LineSegment StartX=-100 StartY=-10 StartZ=0 EndX=-100 EndY=-45 EndZ=0
    g2: LineSegment StartX=-100 StartY=-45 StartZ=0 EndX=60 EndY=-45 EndZ=0
    g3: LineSegment StartX=60 StartY=-45 StartZ=0 EndX=60 EndY=-10 EndZ=0
    g4: LineSegment StartX=60 StartY=-10 StartZ=0 EndX=70 EndY=-10 EndZ=0
    g5: LineSegment StartX=70 StartY=-10 StartZ=0 EndX=70 EndY=-55 EndZ=0
    g6: LineSegment StartX=70 StartY=-55 StartZ=0 EndX=-110 EndY=-55 EndZ=0
    g7: LineSegment StartX=-110 StartY=-55 StartZ=0 EndX=-110 EndY=-10 EndZ=0
    g8: LineSegment [constr] StartX=-110 StartY=-10 StartZ=0 EndX=70 EndY=-10 EndZ=0
    g9: LineSegment [constr] StartX=-100 StartY=-45 StartZ=0 EndX=-100 EndY=-55 EndZ=0
  constraints (29):
    c: Coincident(g0,g1)
    c: Vertical(g1)
    c: Coincident(g1,g2)
    c: Horizontal(g2)
    c: Coincident(g2,g3)
    c: Vertical(g3)
    c: Coincident(g3,g4)
    c: Horizontal(g4)
    c: Coincident(g4,g5)
    c: Vertical(g5)
    c: Coincident(g5,g6)
    c: Horizontal(g6)
    c: Coincident(g6,g7)
    c: Coincident(g7,g0)
    c: Vertical(g7)
    c: Parallel(g0,g-1)
    c: DistanceX(g0,g0) = 10
    c: Equal(g0,g4)
    c: Coincident(g8,g0)
    c: Coincident(g8,g4)
    c: Coincident(g9,g1)
    c: PointOnObject(g9,g6)
    c: Parallel(g9,g-2)
    c: Equal(g0,g9)
    c: DistanceX(g0,g4) = 180
    c: Distance(g0,g-1) = 10
    c: DistanceY(g1,g0) = 35
    c: DistanceX(g6,g-1) = 110
    c: PointOnObject(g3,g8)
FEATURE [PartDesign::Pad] Pad033
  Direction = (0,-1,2e-16)
  Length = 150
  Length2 = 10
  Midplane = true
  Placement = pos=(0,0,0) rot=(1,0,0;1.5708rad)
  Profile = -> Sketch039
  ReferenceAxis = -> Sketch039 [N_Axis]
  Refine = true
  Suppressed = false
  Type = 0
  expr: Length = VarSet.Base_base_y
FEATURE [Sketcher::SketchObject] Sketch040  label="hole"
  ArcFitTolerance = 1e-06
  AttachmentSupport = -> [Plane002]
  ExternalTypes = [1,1,1,1]
  FullyConstrained = true
  MakeInternals = false
  MapMode = 5
  Placement = pos=(0,0,-10) rot=(0,0,1;0rad)
  expr: Constraints[20] = VarSet.Base_m3_insert
  expr: Constraints[30] = VarSet.Base_base_y
  expr: Constraints[31] = VarSet.Base_base_x
  expr: Constraints[32] = VarSet.Base_base_x_small
  sketch-geometry (15):
    g0: LineSegment [constr] StartX=-105 StartY=70 StartZ=0 EndX=-105 EndY=-70 EndZ=0
    g1: LineSegment [constr] StartX=-105 StartY=-70 StartZ=0 EndX=65 EndY=-70 EndZ=0
    g2: LineSegment [constr] StartX=65 StartY=-70 StartZ=0 EndX=65 EndY=70 EndZ=0
    g3: LineSegment [constr] StartX=65 StartY=70 StartZ=0 EndX=-105 EndY=70 EndZ=0
    g4: GeomPoint [constr] X=0 Y=0 Z=0
    g5: Circle CenterX=-105 CenterY=70 CenterZ=0 NormalX=0 NormalY=0 NormalZ=1 AngleXU=0 Radius=2.1
    g6: Circle CenterX=-105 CenterY=5e-15 CenterZ=0 NormalX=0 NormalY=0 NormalZ=1 AngleXU=0 Radius=2.1
    g7: Circle CenterX=-105 CenterY=-70 CenterZ=0 NormalX=0 NormalY=0 NormalZ=1 AngleXU=0 Radius=2.1
    g8: Circle CenterX=65 CenterY=-70 CenterZ=0 NormalX=0 NormalY=0 NormalZ=1 AngleXU=0 Radius=2.1
    g9: Circle CenterX=65 CenterY=0 CenterZ=0 NormalX=0 NormalY=0 NormalZ=1 AngleXU=0 Radius=2.1
    g10: Circle CenterX=65 CenterY=70 CenterZ=0 NormalX=0 NormalY=0 NormalZ=1 AngleXU=0 Radius=2.1
    g11: LineSegment [constr] StartX=-110 StartY=75 StartZ=0 EndX=-110 EndY=-75 EndZ=0
    g12: LineSegment [constr] StartX=-110 StartY=-75 StartZ=0 EndX=70 EndY=-75 EndZ=0
    g13: LineSegment [constr] StartX=70 StartY=-75 StartZ=0 EndX=70 EndY=75 EndZ=0
    g14: LineSegment [constr] StartX=70 StartY=75 StartZ=0 EndX=-110 EndY=75 EndZ=0
  constraints (36):
    c: Coincident(g0,g1)
    c: Coincident(g1,g2)
    c: Coincident(g2,g3)
    c: Coincident(g3,g0)
    c: Vertical(g0)
    c: Vertical(g2)
    c: Horizontal(g1)
    c: Horizontal(g3)
    c: Coincident(g4,g-1)
    c: Coincident(g5,g0)
    c: Symmetric(g0,g0,g6)
    c: Coincident(g7,g0)
    c: Coincident(g8,g1)
    c: Symmetric(g2,g2,g9)
    c: Coincident(g10,g2)
    c: Equal(g5,g6)
    c: Equal(g6,g7)
    c: Equal(g7,g8)
    c: Equal(g8,g9)
    c: Equal(g9,g10)
    c: Diameter(g5) = 4.2
    c: PointOnObject(g9,g-1)
    c: Coincident(g11,g12)
    c: Coincident(g12,g13)
    c: Coincident(g13,g14)
    c: Coincident(g14,g11)
    c: Vertical(g13)
    c: Horizontal(g12)
    c: Horizontal(g14)
    c: Symmetric(g11,g11,g-1)
    c: DistanceY(g11,g11) = 150
    c: DistanceX(g11,g13) = 180
    c: DistanceX(g11,g-1) = 110
    c: Distance(g0,g11) = 5
    c: DistanceY(g0,g11) = 5
    c: DistanceX(g2,g13) = 5
FEATURE [PartDesign::Pocket] Pocket024
  BaseFeature = -> Pad033
  Direction = (0,0,-1)
  Length = 10
  Length2 = 5
  Placement = pos=(0,0,0) rot=(1,0,0;1.5708rad)
  Profile = -> Sketch040
  ReferenceAxis = -> Sketch040 [N_Axis]
  Refine = true
  Suppressed = false
  Type = 0
FEATURE [Sketcher::SketchObject] Sketch044  label="tripode_mount"
  ArcFitTolerance = 1e-06
  AttachmentSupport = -> [Pocket024]
  ExternalTypes = [0]
  FullyConstrained = true
  MakeInternals = false
  MapMode = 5
  Placement = pos=(0,-2.42e-14,-55) rot=(1,0,0;3.14159rad)
  expr: Constraints[34] = VarSet.Base_base_y
  expr: Constraints[35] = VarSet.Base_base_x
  expr: Constraints[36] = VarSet.Base_base_x_small
  expr: Constraints[38] = VarSet.Base_base_x / 2
  sketch-geometry (18):
    g0: LineSegment StartX=-61 StartY=26 StartZ=0 EndX=-61 EndY=-26 EndZ=0
    g1: LineSegment StartX=-56 StartY=-31 StartZ=0 EndX=16 EndY=-31 EndZ=0
    g2: LineSegment StartX=21 StartY=-26 StartZ=0 EndX=21 EndY=26 EndZ=0
    g3: LineSegment StartX=16 StartY=31 StartZ=0 EndX=-56 EndY=31 EndZ=0
    g4: ArcOfCircle CenterX=-56 CenterY=26 CenterZ=0 NormalX=0 NormalY=0 NormalZ=1 AngleXU=0 Radius=5 StartAngle=1.5708 EndAngle=3.14159
    g5: ArcOfCircle CenterX=-56 CenterY=-26 CenterZ=0 NormalX=0 NormalY=0 NormalZ=1 AngleXU=0 Radius=5 StartAngle=3.14159 EndAngle=4.71239
    g6: ArcOfCircle CenterX=16 CenterY=-26 CenterZ=0 NormalX=0 NormalY=0 NormalZ=1 AngleXU=0 Radius=5 StartAngle=4.71239 EndAngle=6.28319
    g7: ArcOfCircle CenterX=16 CenterY=26 CenterZ=0 NormalX=0 NormalY=0 NormalZ=1 AngleXU=0 Radius=5 StartAngle=0 EndAngle=1.5708
    g8: GeomPoint [constr] X=-61 Y=31 Z=0
    g9: GeomPoint [constr] X=21 Y=-31 Z=0
    g10: Circle CenterX=-20 CenterY=0 CenterZ=0 NormalX=0 NormalY=0 NormalZ=1 AngleXU=0 Radius=3
    g11: LineSegment [constr] StartX=-56 StartY=26 StartZ=0 EndX=16 EndY=-26 EndZ=0
    g12: LineSegment [constr] StartX=-110 StartY=75 StartZ=0 EndX=-110 EndY=-75 EndZ=0
    g13: LineSegment [constr] StartX=-110 StartY=-75 StartZ=0 EndX=70 EndY=-75 EndZ=0
    g14: LineSegment [constr] StartX=70 StartY=-75 StartZ=0 EndX=70 EndY=75 EndZ=0
    g15: LineSegment [constr] StartX=70 StartY=75 StartZ=0 EndX=-110 EndY=75 EndZ=0
    g16: Circle CenterX=-27 CenterY=0 CenterZ=0 NormalX=0 NormalY=0 NormalZ=1 AngleXU=0 Radius=3
    g17: Circle CenterX=-13 CenterY=0 CenterZ=0 NormalX=0 NormalY=0 NormalZ=1 AngleXU=0 Radius=3
  constraints (45):
    c: Tangent(g0,g4) = -1.5708
    c: Tangent(g0,g5) = -1.5708
    c: Tangent(g1,g5) = -1.5708
    c: Tangent(g1,g6) = -1.5708
    c: Tangent(g2,g6) = -1.5708
    c: Tangent(g2,g7) = -1.5708
    c: Tangent(g3,g7) = -1.5708
    c: Tangent(g3,g4) = -1.5708
    c: Vertical(g0)
    c: Vertical(g2)
    c: Horizontal(g1)
    c: Horizontal(g3)
    c: Equal(g4,g5)
    c: PointOnObject(g8,g0)
    c: PointOnObject(g8,g3)
    c: PointOnObject(g9,g1)
    c: PointOnObject(g9,g2)
    c: DistanceX(g8,g9) = 82
    c: DistanceY(g9,g8) = 62
    c: Equal(g4,g7)
    c: Equal(g7,g6)
    c: Radius(g4) = 5
    c: Diameter(g10) = 6
    c: Coincident(g11,g4)
    c: Coincident(g11,g6)
    c: Symmetric(g4,g6,g10)
    c: Coincident(g12,g13)
    c: Coincident(g13,g14)
    c: Coincident(g14,g15)
    c: Coincident(g15,g12)
    c: Vertical(g14)
    c: Horizontal(g13)
    c: Horizontal(g15)
    c: Symmetric(g12,g12,g-1)
    c: DistanceY(g12,g12) = 150
    c: DistanceX(g15,g15) = 180
    c: DistanceX(g12,g-1) = 110
    c: PointOnObject(g10,g-1)
    c: DistanceX(g12,g10) = 90
    c: PointOnObject(g16,g-1)
    c: PointOnObject(g17,g-1)
    c: Equal(g10,g16)
    c: Equal(g16,g17)
    c: Distance(g16,g10) = 1
    c: Distance(g10,g17) = 1
FEATURE [PartDesign::Pocket] Pocket026
  BaseFeature = -> Pocket024
  Direction = (0,0,1)
  Length = 4
  Length2 = 5
  Placement = pos=(0,0,0) rot=(1,0,0;1.5708rad)
  Profile = -> Sketch044 [Edge4,Edge3,Edge2,Edge1,Edge8,Edge7,Edge6,Edge5]
  ReferenceAxis = -> Sketch044 [N_Axis]
  Refine = true
  Suppressed = false
  Type = 0
FEATURE [PartDesign::Hole] Hole007
  BaseFeature = -> Hole005
  CustomThreadClearance = 0
  Depth = 25
  DepthType = 0
  Diameter = 3.6
  DrillForDepth = false
  DrillPoint = 1
  DrillPointAngle = 118
  HoleCutCountersinkAngle = 90
  HoleCutCustomValues = false
  HoleCutDepth = 0
  HoleCutDiameter = 6.7
  HoleCutType = 2
  ModelThread = false
  Profile = -> Sketch [Edge5,Edge4,Edge2,Edge3]
  Refine = true
  Suppressed = false
  Tapered = false
  TaperedAngle = 90
  ThreadClass = 0
  ThreadDepth = 25
  ThreadDepthType = 0
  ThreadDiameter = 3
  ThreadDirection = 0
  ThreadFit = 2
  ThreadSize = 9
  ThreadType = 1
  Threaded = false
  UseCustomThreadClearance = false
FEATURE [PartDesign::Body] Body001  label="base_mount"
  AllowCompound = false
  Group = -> [Sketch001,Pad,Sketch,Pocket009,Sketch019,Pocket010,Sketch023,Pocket014,Pocket015,Sketch024,Pocket016,PolarPattern,Pocket017,Sketch035,Hole005,Hole007]
  Origin = -> Origin003
  Tip = -> Hole007
FEATURE [Sketcher::SketchObject] Sketch064  label="motor_driver"
  ArcFitTolerance = 1e-06
  ExternalTypes = [0]
  FullyConstrained = true
  MakeInternals = false
  MapMode = 5
  Placement = pos=(0,-1.98e-14,-45) rot=(0,0,1;3.14159rad)
  sketch-geometry (24):
    g0: Circle CenterX=15 CenterY=-10 CenterZ=0 NormalX=0 NormalY=0 NormalZ=1 AngleXU=0 Radius=3.4
    g1: Circle CenterX=15 CenterY=-10 CenterZ=0 NormalX=0 NormalY=0 NormalZ=1 AngleXU=0 Radius=1.4
    g2: LineSegment [constr] StartX=15 StartY=-10 StartZ=0 EndX=15 EndY=-47 EndZ=0
    g3: LineSegment [constr] StartX=15 StartY=-47 StartZ=0 EndX=52 EndY=-47 EndZ=0
    g4: LineSegment [constr] StartX=52 StartY=-47 StartZ=0 EndX=52 EndY=-10 EndZ=0
    g5: LineSegment [constr] StartX=52 StartY=-10 StartZ=0 EndX=15 EndY=-10 EndZ=0
    g6: Circle CenterX=52 CenterY=-10 CenterZ=0 NormalX=0 NormalY=0 NormalZ=1 AngleXU=0 Radius=1.4
    g7: Circle CenterX=52 CenterY=-10 CenterZ=0 NormalX=0 NormalY=0 NormalZ=1 AngleXU=0 Radius=3.4
    g8: Circle CenterX=52 CenterY=-47 CenterZ=0 NormalX=0 NormalY=0 NormalZ=1 AngleXU=0 Radius=3.4
    g9: Circle CenterX=52 CenterY=-47 CenterZ=0 NormalX=0 NormalY=0 NormalZ=1 AngleXU=0 Radius=1.4
    g10: Circle CenterX=15 CenterY=-47 CenterZ=0 NormalX=0 NormalY=0 NormalZ=1 AngleXU=0 Radius=3.4
    g11: Circle CenterX=15 CenterY=-47 CenterZ=0 NormalX=0 NormalY=0 NormalZ=1 AngleXU=0 Radius=1.4
    g12: Circle CenterX=15 CenterY=47 CenterZ=0 NormalX=0 NormalY=0 NormalZ=1 AngleXU=0 Radius=3.4
    g13: Circle CenterX=15 CenterY=47 CenterZ=0 NormalX=0 NormalY=0 NormalZ=1 AngleXU=0 Radius=1.4
    g14: LineSegment [constr] StartX=15 StartY=47 StartZ=0 EndX=15 EndY=10 EndZ=0
    g15: LineSegment [constr] StartX=15 StartY=10 StartZ=0 EndX=52 EndY=10 EndZ=0
    g16: LineSegment [constr] StartX=52 StartY=10 StartZ=0 EndX=52 EndY=47 EndZ=0
    g17: LineSegment [constr] StartX=52 StartY=47 StartZ=0 EndX=15 EndY=47 EndZ=0
    g18: Circle CenterX=52 CenterY=47 CenterZ=0 NormalX=0 NormalY=0 NormalZ=1 AngleXU=0 Radius=1.4
    g19: Circle CenterX=52 CenterY=47 CenterZ=0 NormalX=0 NormalY=0 NormalZ=1 AngleXU=0 Radius=3.4
    g20: Circle CenterX=52 CenterY=10 CenterZ=0 NormalX=0 NormalY=0 NormalZ=1 AngleXU=0 Radius=3.4
    g21: Circle CenterX=52 CenterY=10 CenterZ=0 NormalX=0 NormalY=0 NormalZ=1 AngleXU=0 Radius=1.4
    g22: Circle CenterX=15 CenterY=10 CenterZ=0 NormalX=0 NormalY=0 NormalZ=1 AngleXU=0 Radius=3.4
    g23: Circle CenterX=15 CenterY=10 CenterZ=0 NormalX=0 NormalY=0 NormalZ=1 AngleXU=0 Radius=1.4
  constraints (55):
    c: Coincident(g1,g0)
    c: Coincident(g2,g3)
    c: Coincident(g3,g4)
    c: Coincident(g4,g5)
    c: Coincident(g5,g2)
    c: Vertical(g2)
    c: Vertical(g4)
    c: Horizontal(g3)
    c: Horizontal(g5)
    c: Coincident(g2,g0)
    c: DistanceX(g0,g4) = 37
    c: DistanceY(g2,g0) = 37
    c: Diameter(g1) = 2.8
    c: Distance(g1,g0) = 2
    c: Coincident(g6,g4)
    c: Coincident(g7,g4)
    c: Coincident(g8,g3)
    c: Coincident(g9,g3)
    c: Coincident(g10,g2)
    c: Coincident(g11,g2)
    c: Equal(g1,g6)
    c: Equal(g6,g9)
    c: Equal(g9,g11)
    c: Equal(g0,g7)
    c: Equal(g7,g8)
    c: Equal(g8,g10)
    c: Coincident(g13,g12)
    c: Coincident(g14,g15)
    c: Coincident(g15,g16)
    c: Coincident(g16,g17)
    c: Coincident(g17,g14)
    c: Vertical(g14)
    c: Vertical(g16)
    c: Horizontal(g15)
    c: Horizontal(g17)
    c: Coincident(g14,g12)
    c: DistanceX(g12,g16) = 37
    c: DistanceY(g14,g12) = 37
    c: Diameter(g13) = 2.8
    c: Distance(g13,g12) = 2
    c: Coincident(g18,g16)
    c: Coincident(g19,g16)
    c: Coincident(g20,g15)
    c: Coincident(g21,g15)
    c: Coincident(g22,g14)
    c: Coincident(g23,g14)
    c: Equal(g13,g18)
    c: Equal(g18,g21)
    c: Equal(g21,g23)
    c: Equal(g12,g19)
    c: Equal(g19,g20)
    c: Equal(g20,g22)
    c: DistanceY(g-1,g15) = 10
    c: Symmetric(g15,g4,g-1)
    c: DistanceX(g-1,g12) = 15
FEATURE [PartDesign::Pad] Pad046
  BaseFeature = -> Pocket026
  Direction = (0,0,1)
  Length = 2
  Length2 = 10
  Placement = pos=(0,0,0) rot=(1,0,0;1.5708rad)
  Profile = -> Sketch064
  ReferenceAxis = -> Sketch064 [N_Axis]
  Refine = true
  Suppressed = false
  Type = 0
FEATURE [PartDesign::Pocket] Pocket042
  BaseFeature = -> Pad046
  Direction = (0,0,-1)
  Length = 5
  Length2 = 5
  Placement = pos=(0,0,0) rot=(1,0,0;1.5708rad)
  Profile = -> Pad046 [Edge91,Edge93,Edge94,Edge92,Edge95,Edge97,Edge96,Edge98]
  Refine = true
  Suppressed = false
  Type = 1
FEATURE [Sketcher::SketchObject] Sketch065  label="center_poles"
  ArcFitTolerance = 1e-06
  AttachmentOffset = pos=(0,0,-45) rot=(0,0,1;0rad)
  AttachmentSupport = -> [XY_Plane024]
  ExternalTypes = [0]
  FullyConstrained = true
  MakeInternals = false
  MapMode = 5
  Placement = pos=(0,0,-45) rot=(0,0,1;0rad)
  expr: Constraints[30] = VarSet.Base_base_y
  expr: Constraints[31] = VarSet.Base_base_x
  expr: Constraints[32] = VarSet.Base_base_x_small
  expr: Constraints[35] = VarSet.Base_base_x / 2
  sketch-geometry (14):
    g0: LineSegment StartX=-32.5 StartY=75 StartZ=0 EndX=-7.5 EndY=75 EndZ=0
    g1: LineSegment StartX=-7.5 StartY=75 StartZ=0 EndX=-7.5 EndY=65 EndZ=0
    g2: LineSegment StartX=-7.5 StartY=65 StartZ=0 EndX=-32.5 EndY=65 EndZ=0
    g3: LineSegment StartX=-32.5 StartY=65 StartZ=0 EndX=-32.5 EndY=75 EndZ=0
    g4: GeomPoint [constr] X=-20 Y=70 Z=0
    g5: LineSegment StartX=-7.5 StartY=-65 StartZ=0 EndX=-7.5 EndY=-75 EndZ=0
    g6: LineSegment StartX=-7.5 StartY=-75 StartZ=0 EndX=-32.5 EndY=-75 EndZ=0
    g7: LineSegment StartX=-32.5 StartY=-75 StartZ=0 EndX=-32.5 EndY=-65 EndZ=0
    g8: LineSegment StartX=-32.5 StartY=-65 StartZ=0 EndX=-7.5 EndY=-65 EndZ=0
    g9: GeomPoint [constr] X=-20 Y=-70 Z=0
    g10: LineSegment [constr] StartX=-110 StartY=75 StartZ=0 EndX=-110 EndY=-75 EndZ=0
    g11: LineSegment [constr] StartX=-110 StartY=-75 StartZ=0 EndX=70 EndY=-75 EndZ=0
    g12: LineSegment [constr] StartX=70 StartY=-75 StartZ=0 EndX=70 EndY=75 EndZ=0
    g13: LineSegment [constr] StartX=70 StartY=75 StartZ=0 EndX=-110 EndY=75 EndZ=0
  constraints (36):
    c: Coincident(g0,g1)
    c: Coincident(g1,g2)
    c: Coincident(g2,g3)
    c: Coincident(g3,g0)
    c: Horizontal(g0)
    c: Horizontal(g2)
    c: Vertical(g1)
    c: Vertical(g3)
    c: Symmetric(g2,g0,g4)
    c: Distance(g1,g3) = 25
    c: Distance(g0,g2) = 10
    c: Coincident(g5,g6)
    c: Coincident(g6,g7)
    c: Coincident(g7,g8)
    c: Coincident(g8,g5)
    c: Vertical(g5)
    c: Vertical(g7)
    c: Horizontal(g6)
    c: Horizontal(g8)
    c: Symmetric(g7,g5,g9)
    c: Equal(g3,g7)
    c: Symmetric(g7,g2,g-1)
    c: Coincident(g10,g11)
    c: Coincident(g11,g12)
    c: Coincident(g12,g13)
    c: Coincident(g13,g10)
    c: Vertical(g12)
    c: Horizontal(g11)
    c: Horizontal(g13)
    c: Symmetric(g10,g10,g-1)
    c: DistanceY(g10,g10) = 150
    c: DistanceX(g10,g12) = 180
    c: Distance(g10,g-2) = 110
    c: PointOnObject(g0,g13)
    c: Equal(g8,g2)
    c: DistanceX(g10,g4) = 90
FEATURE [PartDesign::Pad] Pad047
  BaseFeature = -> Pocket042
  Direction = (0,0,1)
  Length = 35
  Length2 = 10
  Placement = pos=(0,0,0) rot=(1,0,0;1.5708rad)
  Profile = -> Sketch065
  ReferenceAxis = -> Sketch065 [N_Axis]
  Refine = true
  Suppressed = false
  Type = 0
FEATURE [Sketcher::SketchObject] Sketch066  label="center_pole_hole"
  ArcFitTolerance = 1e-06
  AttachmentSupport = -> [XY_Plane024]
  ExternalTypes = [0]
  FullyConstrained = true
  MakeInternals = false
  MapMode = 5
  expr: Constraints[12] = VarSet.Base_base_y
  expr: Constraints[13] = VarSet.Base_base_x_small
  expr: Constraints[14] = VarSet.Base_base_x
  expr: Constraints[15] = VarSet.Base_base_x / 2
  expr: Constraints[1] = VarSet.Base_base_y - 10 mm
  expr: Constraints[3] = VarSet.Base_m3_insert
  sketch-geometry (6):
    g0: Circle CenterX=-20 CenterY=70 CenterZ=0 NormalX=0 NormalY=0 NormalZ=1 AngleXU=0 Radius=2.1
    g1: Circle CenterX=-20 CenterY=-70 CenterZ=0 NormalX=0 NormalY=0 NormalZ=1 AngleXU=0 Radius=2.1
    g2: LineSegment [constr] StartX=-110 StartY=75 StartZ=0 EndX=-110 EndY=-75 EndZ=0
    g3: LineSegment [constr] StartX=-110 StartY=-75 StartZ=0 EndX=70 EndY=-75 EndZ=0
    g4: LineSegment [constr] StartX=70 StartY=-75 StartZ=0 EndX=70 EndY=75 EndZ=0
    g5: LineSegment [constr] StartX=70 StartY=75 StartZ=0 EndX=-110 EndY=75 EndZ=0
  constraints (16):
    c: Symmetric(g1,g0,g-1)
    c: DistanceY(g1,g0) = 140
    c: Equal(g0,g1)
    c: Diameter(g0) = 4.2
    c: Coincident(g2,g3)
    c: Coincident(g3,g4)
    c: Coincident(g4,g5)
    c: Coincident(g5,g2)
    c: Vertical(g4)
    c: Horizontal(g3)
    c: Horizontal(g5)
    c: Symmetric(g2,g2,g-1)
    c: DistanceY(g2,g2) = 150
    c: DistanceX(g2,g-1) = 110
    c: DistanceX(g2,g4) = 180
    c: DistanceX(g2,g0) = 90
FEATURE [PartDesign::Pocket] Pocket043
  BaseFeature = -> Pad047
  Direction = (0,0,-1)
  Length = 30
  Length2 = 5
  Placement = pos=(0,0,0) rot=(1,0,0;1.5708rad)
  Profile = -> Sketch066
  ReferenceAxis = -> Sketch066 [N_Axis]
  Refine = true
  Suppressed = false
  Type = 0
  expr: Length = VarSet.Base_base_thickness + 20 mm
FEATURE [PartDesign::Pocket] Pocket046
  BaseFeature = -> Pocket043
  Direction = (0,0,1)
  Length = 5
  Length2 = 5
  Placement = pos=(0,0,0) rot=(1,0,0;1.5708rad)
  Profile = -> Sketch044 [Edge11,Edge9,Edge10]
  ReferenceAxis = -> Sketch044 [N_Axis]
  Refine = true
  Suppressed = false
  Type = 1
FEATURE [PartDesign::Body] Body013  label="base_mount_down_open"
  AllowCompound = false
  Group = -> [Plane002,Sketch039,Pad033,Sketch040,Pocket024,Sketch044,Pocket026,Sketch064,Pad046,Pocket042,Sketch065,Pad047,Sketch066,Pocket043,Pocket046]
  Origin = -> Origin042
  Tip = -> Pocket046
COMPONENT P12 — recipe-attached ("base_el003", modeled in this document).
Construction recipe (the document's own serialized feature program — sketch geometry with constraints, then the solid features built on it; lengths are millimeters unless a unit is written):

FEATURE [Sketcher::SketchObject] Sketch026  label="base002"
  ArcFitTolerance = 1e-06
  AttachmentSupport = -> [XY_Plane020]
  ExternalTypes = [0]
  FullyConstrained = true
  MakeInternals = false
  MapMode = 5
  expr: Constraints[10] = VarSet.Base_vertical_base_base_x_hole * 1.2
  expr: Constraints[11] = VarSet.Base_vertical_base_base_y_hole * 1.2
  expr: Constraints[22] = VarSet.Base_vertical_base_base_x_hole
  expr: Constraints[23] = VarSet.Base_vertical_base_base_y_hole
  expr: Constraints[31] = 3.3 mm + VarSet.Base_tolerance_inside_circle
  sketch-geometry (14):
    g0: LineSegment StartX=-30 StartY=54 StartZ=0 EndX=-30 EndY=-54 EndZ=0
    g1: LineSegment StartX=-30 StartY=-54 StartZ=0 EndX=30 EndY=-54 EndZ=0
    g2: LineSegment StartX=30 StartY=-54 StartZ=0 EndX=30 EndY=54 EndZ=0
    g3: LineSegment StartX=30 StartY=54 StartZ=0 EndX=-30 EndY=54 EndZ=0
    g4: GeomPoint [constr] X=0 Y=0 Z=0
    g5: LineSegment [constr] StartX=-25 StartY=45 StartZ=0 EndX=-25 EndY=-45 EndZ=0
    g6: LineSegment [constr] StartX=-25 StartY=-45 StartZ=0 EndX=25 EndY=-45 EndZ=0
    g7: LineSegment [constr] StartX=25 StartY=-45 StartZ=0 EndX=25 EndY=45 EndZ=0
    g8: LineSegment [constr] StartX=25 StartY=45 StartZ=0 EndX=-25 EndY=45 EndZ=0
    g9: GeomPoint [constr] X=0 Y=0 Z=0
    g10: Circle CenterX=-25 CenterY=45 CenterZ=0 NormalX=0 NormalY=0 NormalZ=1 AngleXU=0 Radius=1.8
    g11: Circle CenterX=25 CenterY=45 CenterZ=0 NormalX=0 NormalY=0 NormalZ=1 AngleXU=0 Radius=1.8
    g12: Circle CenterX=25 CenterY=-45 CenterZ=0 NormalX=0 NormalY=0 NormalZ=1 AngleXU=0 Radius=1.8
    g13: Circle CenterX=-25 CenterY=-45 CenterZ=0 NormalX=0 NormalY=0 NormalZ=1 AngleXU=0 Radius=1.8
  constraints (32):
    c: Coincident(g0,g1)
    c: Coincident(g1,g2)
    c: Coincident(g2,g3)
    c: Coincident(g3,g0)
    c: Vertical(g0)
    c: Vertical(g2)
    c: Horizontal(g1)
    c: Horizontal(g3)
    c: Symmetric(g2,g0,g4)
    c: Coincident(g4,g-1)
    c: DistanceX(g0,g2) = 60
    c: DistanceY(g0,g0) = 108
    c: Coincident(g5,g6)
    c: Coincident(g6,g7)
    c: Coincident(g7,g8)
    c: Coincident(g8,g5)
    c: Vertical(g5)
    c: Vertical(g7)
    c: Horizontal(g6)
    c: Horizontal(g8)
    c: Symmetric(g7,g5,g9)
    c: Coincident(g9,g4)
    c: DistanceX(g5,g7) = 50
    c: Distance(g5,g8) = 90
    c: Coincident(g10,g5)
    c: Coincident(g11,g7)
    c: Coincident(g12,g6)
    c: Coincident(g13,g5)
    c: Equal(g10,g11)
    c: Equal(g11,g12)
    c: Equal(g12,g13)
    c: Diameter(g10) = 3.6
FEATURE [PartDesign::Pad] Pad025
  Direction = (0,0,1)
  Length = 5
  Length2 = 10
  Profile = -> Sketch026
  ReferenceAxis = -> Sketch026 [N_Axis]
  Refine = true
  Suppressed = false
  Type = 0
FEATURE [Sketcher::SketchObject] Sketch027  label="vertical_outine"
  ArcFitTolerance = 1e-06
  AttachmentSupport = -> [YZ_Plane020]
  ExternalTypes = [0]
  FullyConstrained = true
  MakeInternals = false
  MapMode = 5
  Placement = pos=(0,0,0) rot=(0.57735,0.57735,0.57735;2.0944rad)
  expr: Constraints[9] = VarSet.Base_vertical_base_base_y_hole * 1.2
  sketch-geometry (4):
    g0: LineSegment StartX=-54 StartY=0 StartZ=0 EndX=54 EndY=1e-16 EndZ=0
    g1: LineSegment StartX=54 StartY=1e-16 StartZ=0 EndX=54 EndY=90 EndZ=0
    g2: LineSegment StartX=54 StartY=90 StartZ=0 EndX=-54 EndY=90 EndZ=0
    g3: LineSegment StartX=-54 StartY=90 StartZ=0 EndX=-54 EndY=0 EndZ=0
  constraints (11):
    c: Coincident(g0,g1)
    c: Coincident(g1,g2)
    c: Coincident(g2,g3)
    c: Coincident(g3,g0)
    c: Horizontal(g2)
    c: Vertical(g1)
    c: Vertical(g3)
    c: PointOnObject(g0,g-1)
    c: Symmetric(g0,g0,g-2)
    c: DistanceX(g0,g0) = 108
    c: DistanceY(g0,g2) = 90
FEATURE [PartDesign::Pad] Pad026
  BaseFeature = -> Pad025
  Direction = (1,0,0)
  Length = 6
  Length2 = 10
  Profile = -> Sketch027
  ReferenceAxis = -> Sketch027 [N_Axis]
  Refine = true
  Reversed = true
  Suppressed = false
  Type = 0
FEATURE [Sketcher::SketchObject] Sketch028  label="motor_bearing"
  ArcFitTolerance = 1e-06
  AttachmentSupport = -> [YZ_Plane020]
  ExternalGeometry = -> [Pad026]
  ExternalTypes = [0]
  FullyConstrained = true
  MakeInternals = false
  MapMode = 5
  Placement = pos=(0,0,0) rot=(0.57735,0.57735,0.57735;2.0944rad)
  expr: Constraints[16] = 6 mm + VarSet.Base_tolerance_inside_circle
  expr: Constraints[28] = VarSet.Base_bearing_inside_diameter_with_tolerance
  expr: Constraints[30] = VarSet.Base_distance_gear_el
  expr: Constraints[31] = VarSet.Base_bearing_inside_diameter * 1.1
  sketch-geometry (13):
    g0: LineSegment [constr] StartX=-39 StartY=64 StartZ=0 EndX=-39 EndY=46 EndZ=0
    g1: LineSegment [constr] StartX=-39 StartY=46 StartZ=0 EndX=-6 EndY=46 EndZ=0
    g2: LineSegment [constr] StartX=-6 StartY=46 StartZ=0 EndX=-6 EndY=64 EndZ=0
    g3: LineSegment [constr] StartX=-6 StartY=64 StartZ=0 EndX=-39 EndY=64 EndZ=0
    g4: Circle CenterX=-39 CenterY=64 CenterZ=0 NormalX=0 NormalY=0 NormalZ=1 AngleXU=0 Radius=1.5
    g5: Circle CenterX=-6 CenterY=64 CenterZ=0 NormalX=0 NormalY=0 NormalZ=1 AngleXU=0 Radius=1.5
    g6: Circle CenterX=-6 CenterY=46 CenterZ=0 NormalX=0 NormalY=0 NormalZ=1 AngleXU=0 Radius=1.5
    g7: Circle CenterX=-39 CenterY=46 CenterZ=0 NormalX=0 NormalY=0 NormalZ=1 AngleXU=0 Radius=1.5
    g8: Circle CenterX=-30 CenterY=55 CenterZ=0 NormalX=0 NormalY=0 NormalZ=1 AngleXU=0 Radius=3.15
    g9: LineSegment [constr] StartX=-39 StartY=55 StartZ=0 EndX=-6 EndY=55 EndZ=0
    g10: Circle CenterX=27 CenterY=55 CenterZ=0 NormalX=0 NormalY=0 NormalZ=1 AngleXU=0 Radius=17.7
    g11: LineSegment [constr] StartX=-30 StartY=55 StartZ=0 EndX=27 EndY=55 EndZ=0
    g12: Circle CenterX=27 CenterY=55 CenterZ=0 NormalX=0 NormalY=0 NormalZ=1 AngleXU=0 Radius=19.25
  constraints (33):
    c: Coincident(g0,g1)
    c: Coincident(g1,g2)
    c: Coincident(g2,g3)
    c: Coincident(g3,g0)
    c: Vertical(g0)
    c: Vertical(g2)
    c: Horizontal(g1)
    c: Horizontal(g3)
    c: Coincident(g4,g0)
    c: Coincident(g5,g2)
    c: Coincident(g6,g1)
    c: Coincident(g7,g0)
    c: Equal(g4,g5)
    c: Equal(g5,g6)
    c: Equal(g6,g7)
    c: Diameter(g4) = 3
    c: Diameter(g8) = 6.3
    c: DistanceY(g0,g0) = 18
    c: DistanceX(g0,g1) = 33
    c: PointOnObject(g8,g9)
    c: DistanceX(g9,g8) = 9
    c: PointOnObject(g9,g0)
    c: PointOnObject(g9,g2)
    c: Symmetric(g0,g0,g9)
    c: DistanceY(g-1,g8) = 55
    c: Coincident(g11,g8)
    c: Coincident(g11,g10)
    c: PointOnObject(g9,g11)
    c: Diameter(g10) = 35.4
    c: Coincident(g12,g10)
    c: DistanceX(g8,g10) = 57
    c: Diameter(g12) = 38.5
    c: DistanceX(g-3,g0) = 15
FEATURE [PartDesign::Pad] Pad027  label="bearing_base"
  BaseFeature = -> Pad026
  Direction = (1,0,0)
  Length = 2.5
  Length2 = 10
  Profile = -> Sketch028 [Edge7]
  ReferenceAxis = -> Sketch028 [N_Axis]
  Refine = true
  Suppressed = false
  Type = 0
  expr: Length = 2.5 mm
FEATURE [PartDesign::Pad] Pad028  label="bearing_inside"
  BaseFeature = -> Pad027
  Direction = (1,0,0)
  Length = 7.2
  Length2 = 10
  Profile = -> Sketch028 [Edge6]
  ReferenceAxis = -> Sketch028 [N_Axis]
  Refine = true
  Suppressed = false
  Type = 0
  expr: Length = VarSet.Base_bearing_thickness + 2.4 mm
FEATURE [PartDesign::Pocket] Pocket018
  BaseFeature = -> Pad028
  Direction = (-1,0,0)
  Length = 5
  Length2 = 5
  Profile = -> Sketch028 [Edge5]
  ReferenceAxis = -> Sketch028 [N_Axis]
  Refine = true
  Suppressed = false
  Type = 1
FEATURE [PartDesign::Hole] Hole
  BaseFeature = -> Pocket018
  CustomThreadClearance = 0
  Depth = 25
  DepthType = 0
  Diameter = 3.4
  DrillForDepth = false
  DrillPoint = 1
  DrillPointAngle = 118
  HoleCutCountersinkAngle = 90
  HoleCutCustomValues = false
  HoleCutDepth = 0
  HoleCutDiameter = 6.1
  HoleCutType = 2
  ModelThread = false
  Profile = -> Sketch028 [Edge4,Edge1,Edge2,Edge3]
  Refine = true
  Suppressed = false
  Tapered = false
  TaperedAngle = 90
  ThreadClass = 0
  ThreadDepth = 25
  ThreadDepthType = 0
  ThreadDiameter = 3
  ThreadDirection = 0
  ThreadFit = 0
  ThreadSize = 9
  ThreadType = 1
  Threaded = false
  UseCustomThreadClearance = false
FEATURE [Sketcher::SketchObject] Sketch029  label="bearing_cap_hole"
  ArcFitTolerance = 1e-06
  AttachmentSupport = -> [YZ_Plane020]
  ExternalGeometry = -> [Sketch028]
  ExternalTypes = [0]
  FullyConstrained = true
  MakeInternals = false
  MapMode = 5
  Placement = pos=(0,0,0) rot=(0.57735,0.57735,0.57735;2.0944rad)
  expr: Constraints[4] = VarSet.Base_m3_insert
  expr: Constraints[5] = VarSet.Base_bearing_inside_diameter * 0.5
  sketch-geometry (3):
    g0: LineSegment [constr] StartX=0 StartY=55 StartZ=0 EndX=58 EndY=55 EndZ=0
    g1: Circle CenterX=18.25 CenterY=55 CenterZ=0 NormalX=0 NormalY=0 NormalZ=1 AngleXU=0 Radius=2.1
    g2: Circle CenterX=35.75 CenterY=55 CenterZ=0 NormalX=0 NormalY=0 NormalZ=1 AngleXU=0 Radius=2.1
  constraints (9):
    c: PointOnObject(g0,g-2)
    c: Horizontal(g0)
    c: PointOnObject(g1,g0)
    c: Equal(g1,g2)
    c: Diameter(g1) = 4.2
    c: DistanceX(g1,g2) = 17.5
    c: DistanceX(g0,g0) = 58
    c: PointOnObject(g2,g0)
    c: Symmetric(g1,g2,g-3)
FEATURE [PartDesign::Pocket] Pocket019
  BaseFeature = -> Hole
  Direction = (-1,0,0)
  Length = 5
  Length2 = 5
  Midplane = true
  Profile = -> Sketch029
  ReferenceAxis = -> Sketch029 [N_Axis]
  Refine = true
  Suppressed = false
  Type = 1
FEATURE [Part::DatumPlane] Plane
  AttachmentOffset = pos=(0,0,54) rot=(0,0,1;0rad)
  AttachmentSupport = -> [Origin020]
  MapMode = 5
  Placement = pos=(0,-54,1.2e-14) rot=(1,0,0;1.5708rad)
  expr: .AttachmentOffset.Base.x = 0 mm
FEATURE [Sketcher::SketchObject] Sketch034  label="back_base"
  ArcFitTolerance = 1e-06
  AttachmentOffset = pos=(-3,0,0) rot=(0,0,1;0rad)
  AttachmentSupport = -> [Plane]
  ExternalTypes = [0]
  FullyConstrained = true
  MakeInternals = false
  MapMode = 5
  Placement = pos=(-3,-54,1.2e-14) rot=(1,0,0;1.5708rad)
  expr: Constraints[10] = VarSet.Base_vertical_base_base_x_hole / 2
  sketch-geometry (4):
    g0: LineSegment StartX=0 StartY=0 StartZ=0 EndX=-25 EndY=0 EndZ=0
    g1: LineSegment StartX=-25 StartY=0 StartZ=0 EndX=-25 EndY=5 EndZ=0
    g2: LineSegment StartX=-25 StartY=5 StartZ=0 EndX=0 EndY=90 EndZ=0
    g3: LineSegment StartX=0 StartY=90 StartZ=0 EndX=0 EndY=0 EndZ=0
  constraints (11):
    c: PointOnObject(g0,g-1)
    c: Coincident(g0,g1)
    c: Coincident(g1,g2)
    c: PointOnObject(g2,g-2)
    c: Coincident(g2,g3)
    c: Coincident(g3,g-1)
    c: Coincident(g3,g0)
    c: Distance(g1,g-1) = 5
    c: Distance(g3,g3) = 90
    c: Parallel(g1,g-2)
    c: DistanceX(g0,g-1) = 25
FEATURE [PartDesign::Pad] Pad031
  BaseFeature = -> Pocket019
  Direction = (0,-1,2e-16)
  Length = 5
  Length2 = 10
  Profile = -> Sketch034
  ReferenceAxis = -> Sketch034 [N_Axis]
  Refine = true
  Reversed = true
  Suppressed = false
  Type = 0
FEATURE [PartDesign::LinearPattern] LinearPattern
  BaseFeature = -> Pad031
  Direction = -> X_Axis020
  Length = 103
  Mode = 0
  Occurrences = 2
  Offset = 103
  Originals = -> [Pad031]
  Refine = true
  Suppressed = false
  TransformMode = 0
FEATURE [Part::DatumPlane] Plane005
  AttachmentOffset = pos=(0,0,-3) rot=(0,0,1;0rad)
  AttachmentSupport = -> [Origin020]
  MapMode = 5
  Placement = pos=(-3,0,0) rot=(0.57735,0.57735,0.57735;2.0944rad)
FEATURE [Sketcher::SketchObject] Sketch057  label="motor_reses"
  ArcFitTolerance = 1e-06
  AttachmentSupport = -> [Plane005]
  ExternalGeometry = -> [LinearPattern]
  ExternalTypes = [0,0,0,0]
  FullyConstrained = true
  MakeInternals = false
  MapMode = 5
  Placement = pos=(-3,0,0) rot=(0.57735,0.57735,0.57735;2.0944rad)
  sketch-geometry (12):
    g0: LineSegment StartX=1.5 StartY=38 StartZ=0 EndX=1.5 EndY=72 EndZ=0
    g1: LineSegment StartX=1.5 StartY=72 StartZ=0 EndX=-46.5 EndY=72 EndZ=0
    g2: LineSegment StartX=-46.5 StartY=72 StartZ=0 EndX=-46.5 EndY=38 EndZ=0
    g3: LineSegment StartX=-46.5 StartY=38 StartZ=0 EndX=1.5 EndY=38 EndZ=0
    g4: LineSegment [constr] StartX=-6 StartY=46 StartZ=0 EndX=-39 EndY=64 EndZ=0
    g5: LineSegment [constr] StartX=1.5 StartY=38 StartZ=0 EndX=-46.5 EndY=72 EndZ=0
    g6: GeomPoint [constr] X=-22.5 Y=55 Z=0
    g7: GeomPoint [constr] X=-22.5 Y=55 Z=0
    g8: LineSegment StartX=1.5 StartY=70 StartZ=0 EndX=1.5 EndY=44 EndZ=0
    g9: LineSegment StartX=1.5 StartY=44 StartZ=0 EndX=32.5 EndY=44 EndZ=0
    g10: LineSegment StartX=32.5 StartY=44 StartZ=0 EndX=32.5 EndY=70 EndZ=0
    g11: LineSegment StartX=32.5 StartY=70 StartZ=0 EndX=1.5 EndY=70 EndZ=0
  constraints (29):
    c: Coincident(g0,g1)
    c: Coincident(g1,g2)
    c: Coincident(g2,g3)
    c: Coincident(g3,g0)
    c: Vertical(g0)
    c: Vertical(g2)
    c: Horizontal(g1)
    c: Horizontal(g3)
    c: Distance(g0,g2) = 48
    c: Distance(g1,g3) = 34
    c: Coincident(g4,g-4)
    c: Coincident(g5,g0)
    c: Coincident(g5,g1)
    c: Symmetric(g5,g5,g6)
    c: Symmetric(g4,g4,g7)
    c: Coincident(g6,g7)
    c: Coincident(g4,g-6)
    c: Coincident(g8,g9)
    c: Coincident(g9,g10)
    c: Coincident(g10,g11)
    c: Coincident(g11,g8)
    c: Vertical(g8)
    c: Vertical(g10)
    c: Horizontal(g9)
    c: Horizontal(g11)
    c: Distance(g8,g10) = 31
    c: Distance(g9,g11) = 26
    c: PointOnObject(g8,g0)
    c: Distance(g0,g8) = 2
FEATURE [PartDesign::Pocket] Pocket
  BaseFeature = -> LinearPattern
  Direction = (-1,0,0)
  Length = 4
  Length2 = 5
  Profile = -> Sketch057
  ReferenceAxis = -> Sketch057 [N_Axis]
  Refine = true
  Suppressed = false
  Type = 0
FEATURE [PartDesign::Body] Body010  label="base_el002"
  AllowCompound = false
  Group = -> [Sketch026,Pad025,Sketch027,Pad026,Sketch028,Pad027,Pad028,Pocket018,Hole,Sketch029,Pocket019,Sketch034,Plane,Pad031,LinearPattern,Plane005,Sketch057,Pocket]
  Origin = -> Origin020
  Tip = -> Pocket
COMPONENT P13 — recipe-attached ("bearing_cap_inside_az", modeled in this document).
Construction recipe (the document's own serialized feature program — sketch geometry with constraints, then the solid features built on it; lengths are millimeters unless a unit is written):

FEATURE [Sketcher::SketchObject] Sketch012
  ArcFitTolerance = 1e-06
  AttachmentSupport = -> [XY_Plane014]
  ExternalTypes = [0]
  FullyConstrained = false
  MakeInternals = false
  MapMode = 5
  expr: Constraints[0] = VarSet.Base_bearing_inside_diameter
  expr: Constraints[1] = VarSet.Base_bearing_inside_diameter * 1.1
  sketch-geometry (2):
    g0: Circle CenterX=0 CenterY=0 CenterZ=0 NormalX=0 NormalY=0 NormalZ=1 AngleXU=0 Radius=17.5
    g1: Circle CenterX=0 CenterY=0 CenterZ=0 NormalX=0 NormalY=0 NormalZ=1 AngleXU=0 Radius=19.25
  constraints (2):
    c: Diameter(g0) = 35
    c: Diameter(g1) = 38.5
FEATURE [PartDesign::Pad] Pad017
  Direction = (0,0,1)
  Length = 0.2
  Length2 = 10
  Profile = -> Sketch012 [Edge1]
  ReferenceAxis = -> Sketch012 [N_Axis]
  Refine = true
  Reversed = true
  Suppressed = false
  Type = 0
FEATURE [PartDesign::Pad] Pad018
  BaseFeature = -> Pad017
  Direction = (0,0,1)
  Length = 4
  Length2 = 10
  Profile = -> Sketch012 [Edge2]
  ReferenceAxis = -> Sketch012 [N_Axis]
  Refine = true
  Suppressed = false
  Type = 0
FEATURE [Sketcher::SketchObject] Sketch013
  ArcFitTolerance = 1e-06
  AttachmentSupport = -> [Pad018]
  ExternalTypes = [0]
  FullyConstrained = true
  MakeInternals = false
  MapMode = 5
  Placement = pos=(0,0,4) rot=(0,0,1;0rad)
  expr: Constraints[3] = VarSet.Base_bearing_inside_diameter * 0.5
  sketch-geometry (2):
    g0: Circle CenterX=-8.75 CenterY=0 CenterZ=0 NormalX=0 NormalY=0 NormalZ=1 AngleXU=0 Radius=1.5
    g1: Circle CenterX=8.75 CenterY=0 CenterZ=0 NormalX=0 NormalY=0 NormalZ=1 AngleXU=0 Radius=1.5
  constraints (5):
    c: PointOnObject(g0,g-1)
    c: Equal(g0,g1)
    c: Symmetric(g0,g1,g-2)
    c: DistanceX(g0,g1) = 17.5
    c: Diameter(g0) = 3
FEATURE [PartDesign::Hole] Hole002
  BaseFeature = -> Pad018
  CustomThreadClearance = 0
  Depth = 110.123
  DepthType = 1
  Diameter = 3.4
  DrillForDepth = false
  DrillPoint = 1
  DrillPointAngle = 118
  HoleCutCountersinkAngle = 90
  HoleCutCustomValues = false
  HoleCutDepth = 0
  HoleCutDiameter = 6.1
  HoleCutType = 2
  ModelThread = false
  Profile = -> Sketch013
  Refine = true
  Suppressed = false
  Tapered = false
  TaperedAngle = 90
  ThreadClass = 0
  ThreadDepth = 110.123
  ThreadDepthType = 0
  ThreadDiameter = 3
  ThreadDirection = 0
  ThreadFit = 0
  ThreadSize = 9
  ThreadType = 1
  Threaded = false
  UseCustomThreadClearance = false
FEATURE [PartDesign::Body] Body008  label="bearing_cap001"
  AllowCompound = false
  Group = -> [Sketch012,Pad017,Pad018,Sketch013,Hole002]
  Origin = -> Origin014
  Tip = -> Hole002
COMPONENT P14 — same part as P13; its construction recipe is shown at P13.
COMPONENT P15 — recipe-attached ("bearing_cap_outside_az", modeled in this document).
Construction recipe (the document's own serialized feature program — sketch geometry with constraints, then the solid features built on it; lengths are millimeters unless a unit is written):

FEATURE [Sketcher::SketchObject] Sketch042  label="bearing_cap_outside_main"
  ArcFitTolerance = 1e-06
  AttachmentSupport = -> [XY_Plane026]
  ExternalTypes = [0]
  FullyConstrained = true
  MakeInternals = false
  MapMode = 5
  expr: Constraints[1] = VarSet.Base_bearing_cap_outside_diameter - VarSet.Base_tolerance_outside_circle
  expr: Constraints[3] = VarSet.Base_bearing_inside_diameter * 1.15
  sketch-geometry (2):
    g0: Circle CenterX=0 CenterY=0 CenterZ=0 NormalX=0 NormalY=0 NormalZ=1 AngleXU=0 Radius=30.6
    g1: Circle CenterX=0 CenterY=0 CenterZ=0 NormalX=0 NormalY=0 NormalZ=1 AngleXU=0 Radius=20.125
  constraints (4):
    c: Coincident(g0,g-1)
    c: Diameter(g0) = 61.2
    c: Coincident(g1,g0)
    c: Diameter(g1) = 40.25
FEATURE [PartDesign::Pad] Pad034
  Direction = (0,0,1)
  Length = 2
  Length2 = 10
  Profile = -> Sketch042
  ReferenceAxis = -> Sketch042 [N_Axis]
  Refine = true
  Reversed = true
  Suppressed = false
  Type = 0
FEATURE [Sketcher::SketchObject] Sketch043  label="bearing_cap_outside_hole"
  ArcFitTolerance = 1e-06
  AttachmentSupport = -> [XY_Plane026]
  ExternalTypes = [0]
  FullyConstrained = true
  MakeInternals = false
  MapMode = 5
  expr: Constraints[2] = VarSet.Base_bearing_cap_outside_diameter_hole
  sketch-geometry (1):
    g0: Circle CenterX=0 CenterY=26.4 CenterZ=0 NormalX=0 NormalY=0 NormalZ=1 AngleXU=0 Radius=1.5
  constraints (3):
    c: PointOnObject(g0,g-2)
    c: Diameter(g0) = 3
    c: DistanceY(g-1,g0) = 26.4
FEATURE [PartDesign::Hole] Hole006
  BaseFeature = -> Pad034
  CustomThreadClearance = 0
  Depth = 25
  DepthType = 0
  Diameter = 3.4
  DrillForDepth = false
  DrillPoint = 1
  DrillPointAngle = 118
  HoleCutCountersinkAngle = 90
  HoleCutCustomValues = false
  HoleCutDepth = 0
  HoleCutDiameter = 6.1
  HoleCutType = 2
  ModelThread = false
  Profile = -> Sketch043
  Refine = true
  Suppressed = false
  Tapered = false
  TaperedAngle = 90
  ThreadClass = 0
  ThreadDepth = 25
  ThreadDepthType = 0
  ThreadDiameter = 3
  ThreadDirection = 0
  ThreadFit = 0
  ThreadSize = 9
  ThreadType = 1
  Threaded = false
  UseCustomThreadClearance = false
FEATURE [PartDesign::PolarPattern] PolarPattern002
  Angle = 360
  Axis = -> Sketch043 [N_Axis]
  BaseFeature = -> Hole006
  Mode = 0
  Occurrences = 4
  Offset = 120
  Originals = -> [Hole006]
  Refine = true
  Suppressed = false
  TransformMode = 0
FEATURE [PartDesign::Body] Body014  label="bearing_cap_outside001"
  AllowCompound = false
  Group = -> [Sketch042,Pad034,Sketch043,Hole006,PolarPattern002]
  Origin = -> Origin046
  Tip = -> PolarPattern002
COMPONENT P16 — same part as P15; its construction recipe is shown at P15.
COMPONENT P17 — recipe-attached ("sensor_calibration_helper001", modeled in this document).
Construction recipe (the document's own serialized feature program — sketch geometry with constraints, then the solid features built on it; lengths are millimeters unless a unit is written):

FEATURE [Sketcher::SketchObject] Sketch068
  ArcFitTolerance = 1e-06
  AttachmentSupport = -> [XY_Plane044]
  ExternalTypes = [0]
  FullyConstrained = true
  MakeInternals = false
  MapMode = 5
  sketch-geometry (16):
    g0: LineSegment StartX=-4 StartY=50 StartZ=0 EndX=-4 EndY=-50 EndZ=0
    g1: LineSegment StartX=-4 StartY=-50 StartZ=0 EndX=4 EndY=-50 EndZ=0
    g2: LineSegment StartX=4 StartY=-50 StartZ=0 EndX=4 EndY=50 EndZ=0
    g3: LineSegment StartX=4 StartY=50 StartZ=0 EndX=-4 EndY=50 EndZ=0
    g4: LineSegment [constr] StartX=4 StartY=4 StartZ=0 EndX=-4 EndY=4 EndZ=0
    g5: Circle CenterX=7.55 CenterY=4 CenterZ=0 NormalX=0 NormalY=0 NormalZ=1 AngleXU=0 Radius=1.4
    g6: Circle CenterX=-7.55 CenterY=4 CenterZ=0 NormalX=0 NormalY=0 NormalZ=1 AngleXU=0 Radius=1.4
    g7: Circle CenterX=-7.55 CenterY=4 CenterZ=0 NormalX=0 NormalY=0 NormalZ=1 AngleXU=0 Radius=2.2
    g8: Circle CenterX=7.55 CenterY=4 CenterZ=0 NormalX=0 NormalY=0 NormalZ=1 AngleXU=0 Radius=2.2
    g9: Circle CenterX=0 CenterY=0 CenterZ=0 NormalX=0 NormalY=0 NormalZ=1 AngleXU=0 Radius=2.2
    g10: GeomPoint X=0 Y=4 Z=0
    g11: LineSegment [constr] StartX=0 StartY=4 StartZ=0 EndX=0 EndY=0 EndZ=0
    g12: LineSegment StartX=-50 StartY=6.6 StartZ=0 EndX=-50 EndY=-1.4 EndZ=0
    g13: LineSegment StartX=-50 StartY=-1.4 StartZ=0 EndX=50 EndY=-1.4 EndZ=0
    g14: LineSegment StartX=50 StartY=-1.4 StartZ=0 EndX=50 EndY=6.6 EndZ=0
    g15: LineSegment StartX=50 StartY=6.6 StartZ=0 EndX=-50 EndY=6.6 EndZ=0
  constraints (40):
    c: Coincident(g0,g1)
    c: Coincident(g1,g2)
    c: Coincident(g2,g3)
    c: Coincident(g3,g0)
    c: Vertical(g0)
    c: Horizontal(g3)
    c: DistanceY(g0,g0) = 100
    c: DistanceX(g0,g1) = 8
    c: PointOnObject(g4,g2)
    c: Horizontal(g4)
    c: PointOnObject(g5,g4)
    c: PointOnObject(g6,g4)
    c: Diameter(g6) = 2.8
    c: Coincident(g7,g6)
    c: Coincident(g8,g5)
    c: Equal(g6,g5)
    c: Diameter(g7) = 4.4
    c: Equal(g7,g8)
    c: DistanceX(g6,g5) = 15.1
    c: Equal(g7,g9)
    c: Symmetric(g6,g5,g10)
    c: Coincident(g11,g10)
    c: Vertical(g11)
    c: Coincident(g9,g11)
    c: PointOnObject(g4,g0)
    c: Coincident(g9,g-1)
    c: Symmetric(g0,g1,g-2)
    c: DistanceY(g9,g6) = 4
    c: Symmetric(g1,g2,g-1)
    c: Coincident(g12,g13)
    c: Coincident(g13,g14)
    c: Coincident(g14,g15)
    c: Coincident(g15,g12)
    c: Vertical(g12)
    c: Horizontal(g15)
    c: Symmetric(g12,g13,g-2)
    c: DistanceY(g12,g12) = 8
    c: DistanceX(g12,g14) = 100
    c: Perpendicular(g15,g14)
    c: Distance(g8,g15) = 0.4
FEATURE [PartDesign::Pad] Pad050
  Direction = (0,0,1)
  Length = 3
  Length2 = 10
  Profile = -> Sketch068 [Edge1,Edge11,Edge13,Edge3,Edge4,Edge10,Edge12,Edge2]
  ReferenceAxis = -> Sketch068 [N_Axis]
  Refine = true
  Suppressed = false
  Type = 0
FEATURE [PartDesign::Pad] Pad051
  BaseFeature = -> Pad050
  Direction = (0,0,1)
  Length = 4
  Length2 = 10
  Profile = -> Sketch068 [Edge7,Edge9,Edge8]
  ReferenceAxis = -> Sketch068 [N_Axis]
  Refine = true
  Suppressed = false
  Type = 0
FEATURE [PartDesign::Pocket] Pocket047
  BaseFeature = -> Pad051
  Direction = (0,0,-1)
  Length = 5
  Length2 = 5
  Midplane = true
  Profile = -> Sketch068 [Edge5,Edge6]
  ReferenceAxis = -> Sketch068 [N_Axis]
  Refine = true
  Suppressed = false
  Type = 1
FEATURE [PartDesign::Fillet] Fillet002
  Base = -> Pocket047 [Edge2,Edge34,Edge38,Edge39]
  BaseFeature = -> Pocket047
  Radius = 5
  Refine = true
  SupportTransform = false
  Suppressed = false
  UseAllEdges = false
FEATURE [PartDesign::Body] Body020  label="sensor_calibration_helper"
  AllowCompound = false
  Group = -> [Sketch068,Pad050,Pad051,Pocket047,Fillet002]
  Origin = -> Origin082
  Tip = -> Fillet002
COMPONENT P18 — recipe-attached ("sensor_holder", modeled in this document).
Construction recipe (the document's own serialized feature program — sketch geometry with constraints, then the solid features built on it; lengths are millimeters unless a unit is written):

FEATURE [Sketcher::SketchObject] Sketch069
  ArcFitTolerance = 1e-06
  AttachmentSupport = -> [Origin098]
  ExternalTypes = [0]
  FullyConstrained = true
  MakeInternals = false
  MapMode = 5
  sketch-geometry (6):
    g0: Circle CenterX=-35.355 CenterY=0 CenterZ=0 NormalX=0 NormalY=0 NormalZ=1 AngleXU=0 Radius=1.6
    g1: Circle CenterX=35.355 CenterY=0 CenterZ=0 NormalX=0 NormalY=0 NormalZ=1 AngleXU=0 Radius=1.6
    g2: ArcOfCircle CenterX=-35.355 CenterY=0 CenterZ=0 NormalX=0 NormalY=0 NormalZ=1 AngleXU=0 Radius=10 StartAngle=1.5708 EndAngle=4.71239
    g3: ArcOfCircle CenterX=35.355 CenterY=0 CenterZ=0 NormalX=0 NormalY=0 NormalZ=1 AngleXU=0 Radius=10 StartAngle=4.71239 EndAngle=7.85398
    g4: LineSegment StartX=-35.355 StartY=10 StartZ=0 EndX=35.355 EndY=10 EndZ=0
    g5: LineSegment StartX=-35.355 StartY=-10 StartZ=0 EndX=35.355 EndY=-10 EndZ=0
  constraints (13):
    c: PointOnObject(g0,g-1)
    c: Symmetric(g0,g1,g-2)
    c: Distance(g0,g1) = 70.71
    c: Diameter(g0) = 3.2
    c: Equal(g0,g1)
    c: Tangent(g2,g4) = 1.5708
    c: Tangent(g2,g5) = -1.5708
    c: Tangent(g3,g4) = 1.5708
    c: Tangent(g3,g5) = -1.5708
    c: Equal(g2,g3)
    c: Coincident(g2,g0)
    c: Coincident(g3,g1)
    c: Distance(g5,g4) = 20
FEATURE [PartDesign::Pad] Pad052
  Direction = (0,0,1)
  Length = 3
  Length2 = 10
  Profile = -> Sketch069
  ReferenceAxis = -> Sketch069 [N_Axis]
  Refine = true
  Suppressed = false
  Type = 0
FEATURE [Sketcher::SketchObject] Sketch070
  ArcFitTolerance = 1e-06
  AttachmentOffset = pos=(0,0,-8) rot=(0,0,1;0rad)
  AttachmentSupport = -> [Origin098]
  ExternalTypes = [0]
  FullyConstrained = true
  MakeInternals = false
  MapMode = 5
  Placement = pos=(0,8,-1.8e-15) rot=(1,0,0;1.5708rad)
  sketch-geometry (10):
    g0: LineSegment StartX=-11 StartY=0 StartZ=0 EndX=11 EndY=0 EndZ=0
    g1: LineSegment StartX=11 StartY=0 StartZ=0 EndX=11 EndY=150 EndZ=0
    g2: LineSegment StartX=11 StartY=150 StartZ=0 EndX=-11 EndY=150 EndZ=0
    g3: LineSegment StartX=-11 StartY=150 StartZ=0 EndX=-11 EndY=0 EndZ=0
    g4: LineSegment [constr] StartX=-7.62 StartY=145.5 StartZ=0 EndX=7.62 EndY=145.5 EndZ=0
    g5: Circle CenterX=-7.62 CenterY=145.5 CenterZ=0 NormalX=0 NormalY=0 NormalZ=1 AngleXU=0 Radius=2.5
    g6: Circle CenterX=-7.62 CenterY=145.5 CenterZ=0 NormalX=0 NormalY=0 NormalZ=1 AngleXU=0 Radius=1.45
    g7: Circle CenterX=7.62 CenterY=145.5 CenterZ=0 NormalX=0 NormalY=0 NormalZ=1 AngleXU=0 Radius=2.5
    g8: Circle CenterX=7.62 CenterY=145.5 CenterZ=0 NormalX=0 NormalY=0 NormalZ=1 AngleXU=0 Radius=1.45
    g9: Circle CenterX=0 CenterY=140.5 CenterZ=0 NormalX=0 NormalY=0 NormalZ=1 AngleXU=0 Radius=2.5
  constraints (25):
    c: Coincident(g0,g1)
    c: Coincident(g1,g2)
    c: Coincident(g2,g3)
    c: Coincident(g3,g0)
    c: Horizontal(g0)
    c: Vertical(g1)
    c: Vertical(g3)
    c: PointOnObject(g0,g-1)
    c: DistanceX(g2,g2) = 22
    c: DistanceX(g4,g4) = 15.24
    c: Symmetric(g4,g4,g-2)
    c: Coincident(g5,g4)
    c: Coincident(g6,g4)
    c: Coincident(g7,g4)
    c: Coincident(g8,g4)
    c: Symmetric(g1,g2,g-2)
    c: Equal(g6,g8)
    c: Equal(g5,g7)
    c: Diameter(g6) = 2.9
    c: Diameter(g5) = 5
    c: Distance(g7,g2) = 2
    c: PointOnObject(g9,g-2)
    c: Equal(g7,g9)
    c: DistanceY(g9,g4) = 5
    c: DistanceY(g3,g3) = 150
FEATURE [PartDesign::Pad] Pad053
  BaseFeature = -> Pad052
  Direction = (0,-1,2e-16)
  Length = 4
  Length2 = 10
  Midplane = true
  Profile = -> Sketch070 [Edge3,Edge4,Edge2,Edge1]
  ReferenceAxis = -> Sketch070 [N_Axis]
  Refine = true
  Suppressed = false
  Type = 0
FEATURE [PartDesign::Pad] Pad054
  BaseFeature = -> Pad053
  Direction = (0,-1,2e-16)
  Length = 4
  Length2 = 10
  Profile = -> Sketch070 [Edge5,Edge9,Edge7]
  ReferenceAxis = -> Sketch070 [N_Axis]
  Refine = true
  Suppressed = false
  Type = 0
FEATURE [PartDesign::Pocket] Pocket048
  BaseFeature = -> Pad054
  Direction = (0,1,-2e-16)
  Length = 5
  Length2 = 5
  Midplane = true
  Profile = -> Sketch070 [Edge8,Edge6]
  ReferenceAxis = -> Sketch070 [N_Axis]
  Refine = true
  Suppressed = false
  Type = 1
FEATURE [Sketcher::SketchObject] Sketch071
  ArcFitTolerance = 1e-06
  AttachmentOffset = pos=(0,0,5) rot=(0,0,1;0rad)
  AttachmentSupport = -> [Origin098]
  ExternalGeometry = -> [Pocket048]
  ExternalTypes = [0,0]
  FullyConstrained = true
  MakeInternals = false
  MapMode = 5
  Placement = pos=(5,0,0) rot=(0.57735,0.57735,0.57735;2.0944rad)
  sketch-geometry (4):
    g0: LineSegment StartX=6 StartY=3 StartZ=0 EndX=-10 EndY=3 EndZ=0
    g1: LineSegment StartX=-10 StartY=3 StartZ=0 EndX=2 EndY=113 EndZ=0
    g2: LineSegment StartX=2 StartY=113 StartZ=0 EndX=6 EndY=113 EndZ=0
    g3: LineSegment StartX=6 StartY=113 StartZ=0 EndX=6 EndY=3 EndZ=0
  constraints (10):
    c: Coincident(g-4,g0)
    c: Coincident(g0,g-3)
    c: Coincident(g0,g1)
    c: Coincident(g1,g2)
    c: PointOnObject(g2,g-4)
    c: Horizontal(g2)
    c: Coincident(g2,g3)
    c: Coincident(g3,g0)
    c: Distance(g2,g2) = 4
    c: DistanceY(g3,g3) = 110
FEATURE [PartDesign::Pad] Pad055
  BaseFeature = -> Pocket048
  Direction = (1,0,0)
  Length = 4
  Length2 = 10
  Midplane = true
  Profile = -> Sketch071
  ReferenceAxis = -> Sketch071 [N_Axis]
  Refine = true
  Suppressed = false
  Type = 0
FEATURE [PartDesign::Mirrored] Mirrored001
  BaseFeature = -> Pad055
  MirrorPlane = -> YZ_Plane052
  Originals = -> [Pad055]
  Refine = true
  Suppressed = false
  TransformMode = 0
FEATURE [PartDesign::Body] Body021  label="sensor_holder001"
  AllowCompound = false
  Group = -> [Sketch069,Pad052,Sketch070,Pad053,Pad054,Pocket048,Sketch071,Pad055,Mirrored001]
  Origin = -> Origin098
  Tip = -> Mirrored001
COMPONENT P19 — recipe-attached ("small_spur_gear_double_helix_az", modeled in this document).
Construction recipe (the document's own serialized feature program — sketch geometry with constraints, then the solid features built on it; lengths are millimeters unless a unit is written):

FEATURE [PartDesign::FeaturePython] InvoluteGear005  # WARN: FeaturePython — macro-defined, semantics opaque (R4)
  AttacherType = Attacher::AttachEngine3D
  Suppressed = false
  addendum_diameter = 30
  angular_backlash = 0
  axle_hole = true
  axle_holesize = 6.6
  backlash = 0
  clearance = 0.25
  double_helix = true
  head = 0
  head_fillet = 0.06
  height = 12
  helix_angle = 25
  module = 2.5
  num_teeth = 10
  numpoints = 20
  offset_hole = false
  offset_holeoffset = 10
  offset_holesize = 10
  pitch_diameter = 25
  pressure_angle = 20
  properties_from_tool = false
  reversed_backlash = false
  root_diameter = 18.75
  root_fillet = 0
  shift = 0
  simple = false
  transverse_pitch = 7.85398
  traverse_module = 2.5
  undercut = false
  version = 1.3.0
  expr: angular_backlash = backlash / pitch_diameter * 360 ° / pi
  expr: axle_holesize = VarSet.Base_motor_shaft + 2 * VarSet.Base_tolerance_inside_circle
  expr: height = VarSet.Base_gear_thickness
FEATURE [Sketcher::SketchObject] Sketch047
  ArcFitTolerance = 1e-06
  AttachmentSupport = -> [XY_Plane029]
  ExternalTypes = [0]
  FullyConstrained = true
  MakeInternals = false
  MapMode = 5
  expr: Constraints[0] = VarSet.Base_motor_shaft * 1.2
  expr: Constraints[7] = VarSet.Base_motor_shaft / 2 - 1 mm
  sketch-geometry (4):
    g0: Circle [constr] CenterX=0 CenterY=0 CenterZ=0 NormalX=0 NormalY=0 NormalZ=1 AngleXU=0 Radius=3.6
    g1: ArcOfCircle CenterX=0 CenterY=0 CenterZ=0 NormalX=0 NormalY=0 NormalZ=1 AngleXU=0 Radius=3.6 StartAngle=3.73062 EndAngle=5.69415
    g2: LineSegment StartX=-2.99333 StartY=-2 StartZ=0 EndX=2.99333 EndY=-2 EndZ=0
    g3: LineSegment [constr] StartX=-5 StartY=3.6 StartZ=0 EndX=5 EndY=3.6 EndZ=0
  constraints (12):
    c: Diameter(g0) = 7.2
    c: Coincident(g1,g0)
    c: PointOnObject(g1,g0)
    c: Coincident(g2,g1)
    c: Coincident(g2,g1)
    c: Horizontal(g2)
    c: Coincident(g0,g-1)
    c: DistanceY(g1,g-1) = 2
    c: Distance(g3) = 10
    c: Symmetric(g3,g3,g-2)
    c: DistanceY(g3,g1) = -5.6
    c: Tangent(g3,g0)
FEATURE [Part::DatumPlane] Plane004
  AttachmentOffset = pos=(0,0,20) rot=(0,0,1;0rad)
  AttachmentSupport = -> [Origin052]
  MapMode = 5
  Placement = pos=(0,-20,4.4e-15) rot=(1,0,0;1.5708rad)
FEATURE [Sketcher::SketchObject] Sketch049
  ArcFitTolerance = 1e-06
  AttachmentSupport = -> [Plane004]
  ExternalTypes = [0]
  FullyConstrained = true
  MakeInternals = false
  MapMode = 5
  Placement = pos=(0,-20,4.4e-15) rot=(1,0,0;1.5708rad)
  expr: Constraints[2] = VarSet.Base_gear_thickness / 2
  sketch-geometry (1):
    g0: Circle CenterX=0 CenterY=6 CenterZ=0 NormalX=0 NormalY=0 NormalZ=1 AngleXU=0 Radius=1
  constraints (3):
    c: PointOnObject(g0,g-2)
    c: Diameter(g0) = 2
    c: DistanceY(g-1,g0) = 6
FEATURE [PartDesign::Pad] Pad042
  BaseFeature = -> InvoluteGear005
  Direction = (0,0,1)
  Length = 12
  Length2 = 10
  Profile = -> Sketch047
  ReferenceAxis = -> Sketch047 [N_Axis]
  Refine = true
  Suppressed = false
  Type = 0
  expr: Length = VarSet.Base_gear_thickness
FEATURE [PartDesign::Pocket] Pocket039
  BaseFeature = -> Pad042
  Direction = (0,1,-2e-16)
  Length = 5
  Length2 = 5
  Profile = -> Sketch049
  ReferenceAxis = -> Sketch049 [N_Axis]
  Refine = true
  Suppressed = false
  Type = 1
FEATURE [PartDesign::Body] Body016
  AllowCompound = false
  Group = -> [InvoluteGear005,Sketch047,Plane004,Sketch049,Pad042,Pocket039]
  Origin = -> Origin052
  Tip = -> Pocket039
COMPONENT P20 — same part as P19; its construction recipe is shown at P19.
COMPONENT P21 — recipe-attached ("tolerance_test_print001", modeled in this document).
Construction recipe (the document's own serialized feature program — sketch geometry with constraints, then the solid features built on it; lengths are millimeters unless a unit is written):

FEATURE [Sketcher::SketchObject] Sketch058
  ArcFitTolerance = 1e-06
  AttachmentSupport = -> [XY_Plane036]
  ExternalTypes = [0]
  FullyConstrained = true
  MakeInternals = false
  MapMode = 5
  expr: Constraints[1] = VarSet.Base_bearing_outside_diameter_with_tolerance
  expr: Constraints[23] = VarSet.Base_bearing_inside_diameter_with_tolerance
  sketch-geometry (19):
    g0: Circle CenterX=0 CenterY=0 CenterZ=0 NormalX=0 NormalY=0 NormalZ=1 AngleXU=0 Radius=22.15
    g1: LineSegment StartX=-25.15 StartY=5.15 StartZ=0 EndX=-25.15 EndY=-5.15 EndZ=0
    g2: LineSegment StartX=-5.15 StartY=-25.15 StartZ=0 EndX=42.55 EndY=-25.15 EndZ=0
    g3: LineSegment StartX=62.55 StartY=-5.15 StartZ=0 EndX=62.55 EndY=5.15 EndZ=0
    g4: LineSegment StartX=42.55 StartY=25.15 StartZ=0 EndX=-5.15 EndY=25.15 EndZ=0
    g5: LineSegment [constr] StartX=-22.15 StartY=25.15 StartZ=0 EndX=-22.15 EndY=-25.15 EndZ=0
    g6: LineSegment [constr] StartX=-25.15 StartY=22.15 StartZ=0 EndX=62.55 EndY=22.15 EndZ=0
    g7: LineSegment [constr] StartX=22.15 StartY=25.15 StartZ=0 EndX=22.15 EndY=-25.15 EndZ=0
    g8: LineSegment [constr] StartX=25.15 StartY=25.15 StartZ=0 EndX=25.15 EndY=-25.15 EndZ=0
    g9: LineSegment [constr] StartX=60.55 StartY=25.15 StartZ=0 EndX=60.55 EndY=-25.15 EndZ=0
    g10: Circle CenterX=42.85 CenterY=0 CenterZ=0 NormalX=0 NormalY=0 NormalZ=1 AngleXU=0 Radius=17.7
    g11: ArcOfCircle CenterX=-5.15 CenterY=5.15 CenterZ=0 NormalX=0 NormalY=0 NormalZ=1 AngleXU=0 Radius=20 StartAngle=1.5708 EndAngle=3.14159
    g12: GeomPoint [constr] X=-25.15 Y=25.15 Z=0
    g13: ArcOfCircle CenterX=-5.15 CenterY=-5.15 CenterZ=0 NormalX=0 NormalY=0 NormalZ=1 AngleXU=0 Radius=20 StartAngle=3.14159 EndAngle=4.71239
    g14: GeomPoint [constr] X=-25.15 Y=-25.15 Z=0
    g15: ArcOfCircle CenterX=42.55 CenterY=-5.15 CenterZ=0 NormalX=0 NormalY=0 NormalZ=1 AngleXU=0 Radius=20 StartAngle=4.71239 EndAngle=6.28319
    g16: GeomPoint [constr] X=62.55 Y=-25.15 Z=0
    g17: ArcOfCircle CenterX=42.55 CenterY=5.15 CenterZ=0 NormalX=0 NormalY=0 NormalZ=1 AngleXU=0 Radius=20 StartAngle=0 EndAngle=1.5708
    g18: GeomPoint [constr] X=62.55 Y=25.15 Z=0
  constraints (52):
    c: Coincident(g0,g-1)
    c: Diameter(g0) = 44.3
    c: Vertical(g3)
    c: Horizontal(g2)
    c: Horizontal(g4)
    c: Symmetric(g14,g12,g-1)
    c: PointOnObject(g5,g4)
    c: PointOnObject(g5,g2)
    c: Vertical(g5)
    c: Tangent(g5,g0)
    c: PointOnObject(g6,g1)
    c: PointOnObject(g6,g3)
    c: Horizontal(g6)
    c: Tangent(g0,g6)
    c: Distance(g12,g5) = 3
    c: DistanceY(g6,g12) = 3
    c: PointOnObject(g7,g4)
    c: PointOnObject(g7,g2)
    c: Vertical(g7)
    c: PointOnObject(g8,g4)
    c: Vertical(g8)
    c: PointOnObject(g9,g4)
    c: PointOnObject(g10,g-1)
    c: Diameter(g10) = 35.4
    c: Tangent(g8,g10)
    c: Tangent(g10,g9)
    c: DistanceX(g7,g8) = 3
    c: Tangent(g0,g7)
    c: PointOnObject(g9,g2)
    c: Perpendicular(g-1,g9)
    c: DistanceX(g9,g18) = 2
    c: PointOnObject(g8,g2)
    c: PointOnObject(g12,g1)
    c: PointOnObject(g12,g4)
    c: Tangent(g1,g11) = -1.5708
    c: Tangent(g4,g11) = -1.5708
    c: PointOnObject(g14,g1)
    c: PointOnObject(g14,g2)
    c: Tangent(g1,g13) = -1.5708
    c: Tangent(g2,g13) = -1.5708
    c: PointOnObject(g16,g2)
    c: PointOnObject(g16,g3)
    c: Tangent(g2,g15) = -1.5708
    c: Tangent(g3,g15) = -1.5708
    c: PointOnObject(g18,g4)
    c: PointOnObject(g18,g3)
    c: Tangent(g4,g17) = -1.5708
    c: Tangent(g3,g17) = -1.5708
    c: Equal(g11,g13)
    c: Equal(g11,g15)
    c: Equal(g11,g17)
    c: Radius(g11) = 20
FEATURE [PartDesign::Pad] Pad040
  Direction = (0,0,1)
  Length = 4.8
  Length2 = 10
  Profile = -> Sketch058 [Edge8,Edge7,Edge6,Edge5,Edge4,Edge3,Edge2,Edge9]
  ReferenceAxis = -> Sketch058 [N_Axis]
  Refine = true
  Suppressed = false
  Type = 0
  expr: Length = VarSet.Base_bearing_thickness
FEATURE [PartDesign::Pocket] Pocket038
  BaseFeature = -> Pad040
  Direction = (0,0,-1)
  Length = 5
  Length2 = 5
  Midplane = true
  Profile = -> Sketch058 [Edge1]
  ReferenceAxis = -> Sketch058 [N_Axis]
  Refine = true
  Suppressed = false
  Type = 1
FEATURE [PartDesign::Pad] Pad041
  BaseFeature = -> Pocket038
  Direction = (0,0,1)
  Length = 9.6
  Length2 = 10
  Profile = -> Sketch058 [Edge10]
  ReferenceAxis = -> Sketch058 [N_Axis]
  Refine = true
  Suppressed = false
  Type = 0
  expr: Length = 2 * VarSet.Base_bearing_thickness
FEATURE [PartDesign::Body] Body
  AllowCompound = false
  Group = -> [Sketch058,Pad040,Pocket038,Pad041]
  Origin = -> Origin066
  Tip = -> Pad041
COMPONENT P22 — recipe-attached ("wheel_az_double_helix_az", modeled in this document).
Construction recipe (the document's own serialized feature program — sketch geometry with constraints, then the solid features built on it; lengths are millimeters unless a unit is written):

FEATURE [Sketcher::SketchObject] Sketch050  label="baring_house001"
  ArcFitTolerance = 1e-06
  AttachmentSupport = -> [XY_Plane032]
  ExternalTypes = [0]
  FullyConstrained = true
  MakeInternals = false
  MapMode = 5
  expr: Constraints[2] = VarSet.Base_bearing_inside_diameter_with_tolerance
  expr: Constraints[3] = VarSet.Base_bearing_inside_diameter * 1.1
  sketch-geometry (2):
    g0: Circle CenterX=0 CenterY=0 CenterZ=0 NormalX=0 NormalY=0 NormalZ=1 AngleXU=0 Radius=17.7
    g1: Circle CenterX=0 CenterY=0 CenterZ=0 NormalX=0 NormalY=0 NormalZ=1 AngleXU=0 Radius=19.25
  constraints (4):
    c: Coincident(g0,g-1)
    c: Coincident(g1,g0)
    c: Diameter(g0) = 35.4
    c: Diameter(g1) = 38.5
FEATURE [Sketcher::SketchObject] Sketch051  label="hex_hole_mount"
  ArcFitTolerance = 1e-06
  AttachmentSupport = -> [XY_Plane032]
  ExternalTypes = [0]
  FullyConstrained = true
  MakeInternals = false
  MapMode = 5
  expr: Constraints[10] = VarSet.Base_vertical_base_base_y_hole
  expr: Constraints[19] = 3.5 mm + VarSet.Base_tolerance_inside_circle
  expr: Constraints[98] = 5.8 mm + VarSet.Base_tolerance_inside_circle
  expr: Constraints[9] = VarSet.Base_vertical_base_base_x_hole
  sketch-geometry (37):
    g0: LineSegment [constr] StartX=-25 StartY=-45 StartZ=0 EndX=25 EndY=-45 EndZ=0
    g1: LineSegment [constr] StartX=25 StartY=-45 StartZ=0 EndX=25 EndY=45 EndZ=0
    g2: LineSegment [constr] StartX=25 StartY=45 StartZ=0 EndX=-25 EndY=45 EndZ=0
    g3: LineSegment [constr] StartX=-25 StartY=45 StartZ=0 EndX=-25 EndY=-45 EndZ=0
    g4: GeomPoint [constr] X=0 Y=0 Z=0
    g5: Circle CenterX=-25 CenterY=45 CenterZ=0 NormalX=0 NormalY=0 NormalZ=1 AngleXU=0 Radius=1.9
    g6: Circle CenterX=25 CenterY=45 CenterZ=0 NormalX=0 NormalY=0 NormalZ=1 AngleXU=0 Radius=1.9
    g7: Circle CenterX=25 CenterY=-45 CenterZ=0 NormalX=0 NormalY=0 NormalZ=1 AngleXU=0 Radius=1.9
    g8: Circle CenterX=-25 CenterY=-45 CenterZ=0 NormalX=0 NormalY=0 NormalZ=1 AngleXU=0 Radius=1.9
    g9: LineSegment StartX=-23.2391 StartY=41.95 StartZ=0 EndX=-21.4782 EndY=45 EndZ=0
    g10: LineSegment StartX=-21.4782 StartY=45 StartZ=0 EndX=-23.2391 EndY=48.05 EndZ=0
    g11: LineSegment StartX=-23.2391 StartY=48.05 StartZ=0 EndX=-26.7609 EndY=48.05 EndZ=0
    g12: LineSegment StartX=-26.7609 StartY=48.05 StartZ=0 EndX=-28.5218 EndY=45 EndZ=0
    g13: LineSegment StartX=-28.5218 StartY=45 StartZ=0 EndX=-26.7609 EndY=41.95 EndZ=0
    g14: LineSegment StartX=-26.7609 StartY=41.95 StartZ=0 EndX=-23.2391 EndY=41.95 EndZ=0
    g15: Circle [constr] CenterX=-25 CenterY=45 CenterZ=0 NormalX=0 NormalY=0 NormalZ=1 AngleXU=0 Radius=3.52184
    g16: LineSegment StartX=26.7609 StartY=41.95 StartZ=0 EndX=28.5218 EndY=45 EndZ=0
    g17: LineSegment StartX=28.5218 StartY=45 StartZ=0 EndX=26.7609 EndY=48.05 EndZ=0
    g18: LineSegment StartX=26.7609 StartY=48.05 StartZ=0 EndX=23.2391 EndY=48.05 EndZ=0
    g19: LineSegment StartX=23.2391 StartY=48.05 StartZ=0 EndX=21.4782 EndY=45 EndZ=0
    g20: LineSegment StartX=21.4782 StartY=45 StartZ=0 EndX=23.2391 EndY=41.95 EndZ=0
    g21: LineSegment StartX=23.2391 StartY=41.95 StartZ=0 EndX=26.7609 EndY=41.95 EndZ=0
    g22: Circle [constr] CenterX=25 CenterY=45 CenterZ=0 NormalX=0 NormalY=0 NormalZ=1 AngleXU=0 Radius=3.52184
    g23: LineSegment StartX=23.2391 StartY=-41.95 StartZ=0 EndX=21.4782 EndY=-45 EndZ=0
    g24: LineSegment StartX=21.4782 StartY=-45 StartZ=0 EndX=23.2391 EndY=-48.05 EndZ=0
    g25: LineSegment StartX=23.2391 StartY=-48.05 StartZ=0 EndX=26.7609 EndY=-48.05 EndZ=0
    g26: LineSegment StartX=26.7609 StartY=-48.05 StartZ=0 EndX=28.5218 EndY=-45 EndZ=0
    g27: LineSegment StartX=28.5218 StartY=-45 StartZ=0 EndX=26.7609 EndY=-41.95 EndZ=0
    g28: LineSegment StartX=26.7609 StartY=-41.95 StartZ=0 EndX=23.2391 EndY=-41.95 EndZ=0
    g29: Circle [constr] CenterX=25 CenterY=-45 CenterZ=0 NormalX=0 NormalY=0 NormalZ=1 AngleXU=0 Radius=3.52184
    g30: LineSegment StartX=-23.2391 StartY=-41.95 StartZ=0 EndX=-26.7609 EndY=-41.95 EndZ=0
    g31: LineSegment StartX=-26.7609 StartY=-41.95 StartZ=0 EndX=-28.5218 EndY=-45 EndZ=0
    g32: LineSegment StartX=-28.5218 StartY=-45 StartZ=0 EndX=-26.7609 EndY=-48.05 EndZ=0
    g33: LineSegment StartX=-26.7609 StartY=-48.05 StartZ=0 EndX=-23.2391 EndY=-48.05 EndZ=0
    g34: LineSegment StartX=-23.2391 StartY=-48.05 StartZ=0 EndX=-21.4782 EndY=-45 EndZ=0
    g35: LineSegment StartX=-21.4782 StartY=-45 StartZ=0 EndX=-23.2391 EndY=-41.95 EndZ=0
    g36: Circle [constr] CenterX=-25 CenterY=-45 CenterZ=0 NormalX=0 NormalY=0 NormalZ=1 AngleXU=0 Radius=3.52184
  constraints (84):
    c: Coincident(g0,g1)
    c: Coincident(g1,g2)
    c: Coincident(g2,g3)
    c: Coincident(g3,g0)
    c: Horizontal(g0)
    c: Horizontal(g2)
    c: Vertical(g1)
    c: Vertical(g3)
    c: Symmetric(g2,g0,g4)
    c: Distance(g1,g3) = 50
    c: Distance(g0,g2) = 90
    c: Coincident(g4,g-1)
    c: Coincident(g5,g2)
    c: Coincident(g6,g1)
    c: Coincident(g7,g0)
    c: Coincident(g8,g0)
    c: Equal(g8,g7)
    c: Equal(g7,g6)
    c: Equal(g6,g5)
    c: Diameter(g5) = 3.8
    c: Coincident(g9,g10)
    c: Coincident(g10,g11)
    c: Coincident(g11,g12)
    c: Coincident(g12,g13)
    c: Coincident(g13,g14)
    c: Coincident(g14,g9)
    c: Equal(g9, g10-g14) x5
    c: PointOnObject(g9,g15)
    c: PointOnObject(g10,g15)
    c: PointOnObject(g11,g15)
    c: PointOnObject(g12,g15)
    c: PointOnObject(g13,g15)
    c: PointOnObject(g14,g15)
    c: Coincident(g15,g2)
    c: Coincident(g16,g17)
    c: Coincident(g17,g18)
    c: Coincident(g18,g19)
    c: Coincident(g19,g20)
    c: Coincident(g20,g21)
    c: Coincident(g21,g16)
    c: Equal(g16, g17-g21) x5
    c: PointOnObject(g16,g22)
    c: PointOnObject(g17,g22)
    c: PointOnObject(g18,g22)
    c: PointOnObject(g19,g22)
    c: PointOnObject(g20,g22)
    c: PointOnObject(g21,g22)
    c: Coincident(g22,g1)
    c: Coincident(g23,g24)
    c: Coincident(g24,g25)
    c: Coincident(g25,g26)
    c: Coincident(g26,g27)
    c: Coincident(g27,g28)
    c: Coincident(g28,g23)
    c: Equal(g23, g24-g28) x5
    c: PointOnObject(g23,g29)
    c: PointOnObject(g24,g29)
    c: PointOnObject(g25,g29)
    c: PointOnObject(g26,g29)
    c: PointOnObject(g27,g29)
    c: PointOnObject(g28,g29)
    c: Coincident(g29,g0)
    c: Coincident(g30,g31)
    c: Coincident(g31,g32)
    c: Coincident(g32,g33)
    c: Coincident(g33,g34)
    c: Coincident(g34,g35)
    c: Coincident(g35,g30)
    c: Equal(g30, g31-g35) x5
    c: PointOnObject(g30,g36)
    c: PointOnObject(g31,g36)
    c: PointOnObject(g32,g36)
    c: PointOnObject(g33,g36)
    c: PointOnObject(g34,g36)
    c: PointOnObject(g35,g36)
    c: Coincident(g36,g0)
    c: Parallel(g30,g-1)
    c: Equal(g15,g22)
    c: Equal(g22,g29)
    c: Equal(g29,g36)
    c: Parallel(g28,g-1)
    c: Parallel(g14,g-1)
    c: Distance(g11,g9) = 6.1
    c: Parallel(g21,g-1)
FEATURE [Sketcher::SketchObject] Sketch052  label="bearing_cap_hole001"
  ArcFitTolerance = 1e-06
  AttachmentSupport = -> [XY_Plane032]
  ExternalTypes = [0]
  FullyConstrained = true
  MakeInternals = false
  MapMode = 5
  expr: Constraints[2] = VarSet.Base_m3_insert
  expr: Constraints[4] = VarSet.Base_bearing_inside_diameter * 0.5
  sketch-geometry (2):
    g0: Circle CenterX=-8.75 CenterY=0 CenterZ=0 NormalX=0 NormalY=0 NormalZ=1 AngleXU=0 Radius=2.1
    g1: Circle CenterX=8.75 CenterY=0 CenterZ=0 NormalX=0 NormalY=0 NormalZ=1 AngleXU=0 Radius=2.1
  constraints (5):
    c: PointOnObject(g0,g-1)
    c: Equal(g0,g1)
    c: Diameter(g0) = 4.2
    c: Symmetric(g0,g1,g-2)
    c: DistanceX(g0,g1) = 17.5
FEATURE [PartDesign::FeaturePython] InvoluteGear007  # WARN: FeaturePython — macro-defined, semantics opaque (R4)
  AttacherType = Attacher::AttachEngine3D
  Suppressed = false
  addendum_diameter = 140
  angular_backlash = 0
  axle_hole = false
  axle_holesize = 10
  backlash = 0
  clearance = 0.25
  double_helix = true
  head = 0
  head_fillet = 0.06
  height = 12
  helix_angle = 25
  module = 2.5
  num_teeth = 54
  numpoints = 20
  offset_hole = false
  offset_holeoffset = 10
  offset_holesize = 10
  pitch_diameter = 135
  pressure_angle = 20
  properties_from_tool = false
  reversed_backlash = false
  root_diameter = 128.75
  root_fillet = 0
  shift = 0
  simple = false
  transverse_pitch = 7.85398
  traverse_module = 2.5
  undercut = false
  version = 1.3.0
  expr: angular_backlash = backlash / pitch_diameter * 360 ° / pi
  expr: height = VarSet.Base_gear_thickness
FEATURE [PartDesign::Pad] Pad038
  BaseFeature = -> InvoluteGear007
  Direction = (0,0,1)
  Length = 7.3
  Length2 = 10
  Profile = -> Sketch050 [Edge1]
  ReferenceAxis = -> Sketch050 [N_Axis]
  Refine = true
  Reversed = true
  Suppressed = false
  Type = 0
  expr: Length = VarSet.Base_bearing_thickness + VarSet.Base_wheel_az_offset
FEATURE [PartDesign::Pad] Pad039
  BaseFeature = -> Pad038
  Direction = (0,0,1)
  Length = 2.5
  Length2 = 10
  Profile = -> Sketch050 [Edge2]
  ReferenceAxis = -> Sketch050 [N_Axis]
  Refine = true
  Reversed = true
  Suppressed = false
  Type = 0
  expr: Length = VarSet.Base_wheel_az_offset
FEATURE [PartDesign::Pocket] Pocket029
  BaseFeature = -> Pad039
  Direction = (0,0,-1)
  Length = 5
  Length2 = 5
  Midplane = true
  Profile = -> Sketch052
  ReferenceAxis = -> Sketch052 [N_Axis]
  Refine = true
  Suppressed = false
  Type = 1
FEATURE [PartDesign::Pocket] Pocket030  label="hex001"
  BaseFeature = -> Pocket029
  Direction = (0,0,-1)
  Length = 2.4
  Length2 = 5
  Profile = -> Sketch051 [Edge16,Edge11,Edge12,Vertex13,Edge13,Edge14,Edge15,Edge10,Edge5,Edge6,Edge7,Edge8,Edge9,Edge26,Edge27,Edge28,Edge23,Edge24,Edge25,Edge19,Edge20,Edge21,Edge22,Edge17,Edge18]
  ReferenceAxis = -> Sketch051 [N_Axis]
  Refine = true
  Reversed = true
  Suppressed = false
  Type = 0
FEATURE [PartDesign::Pocket] Pocket031
  BaseFeature = -> Pocket030
  Direction = (0,0,-1)
  Length = 5
  Length2 = 5
  Midplane = true
  Profile = -> Sketch051 [Edge3,Edge4,Edge1,Edge2]
  ReferenceAxis = -> Sketch051 [N_Axis]
  Refine = true
  Suppressed = false
  Type = 1
FEATURE [PartDesign::Body] Body017  label="wheel_az003"
  AllowCompound = false
  Group = -> [Sketch050,Sketch051,Sketch052,InvoluteGear007,Pad038,Pad039,Pocket029,Pocket030,Pocket031]
  Origin = -> Origin057
  Tip = -> Pocket031
COMPONENT P23 — recipe-attached ("wheel_el_double_helix001", modeled in this document).
Construction recipe (the document's own serialized feature program — sketch geometry with constraints, then the solid features built on it; lengths are millimeters unless a unit is written):

FEATURE [Sketcher::SketchObject] Sketch053  label="center_holes"
  ArcFitTolerance = 1e-06
  AttachmentSupport = -> [XY_Plane034]
  ExternalTypes = [0]
  FullyConstrained = true
  MakeInternals = false
  MapMode = 5
  expr: Constraints[1] = VarSet.Base_bearing_outside_diameter_with_tolerance
  expr: Constraints[3] = VarSet.Base_bearing_outside_diameter_inside * 1.02
  expr: Constraints[5] = VarSet.Base_bearing_cap_outside_diameter + VarSet.Base_tolerance_inside_circle
  sketch-geometry (3):
    g0: Circle CenterX=0 CenterY=0 CenterZ=0 NormalX=0 NormalY=0 NormalZ=1 AngleXU=0 Radius=22.15
    g1: Circle CenterX=0 CenterY=0 CenterZ=0 NormalX=0 NormalY=0 NormalZ=1 AngleXU=0 Radius=20.91
    g2: Circle CenterX=0 CenterY=0 CenterZ=0 NormalX=0 NormalY=0 NormalZ=1 AngleXU=0 Radius=30.95
  constraints (6):
    c: Coincident(g0,g-1)
    c: Diameter(g0) = 44.3
    c: Coincident(g1,g0)
    c: Diameter(g1) = 41.82
    c: Coincident(g2,g0)
    c: Diameter(g2) = 61.9
FEATURE [Sketcher::SketchObject] Sketch054  label="hex_center"
  ArcFitTolerance = 1e-06
  AttachmentSupport = -> [XY_Plane034]
  ExternalTypes = [0]
  FullyConstrained = true
  MakeInternals = false
  MapMode = 5
  expr: Constraints[17] = 3.2 mm + VarSet.Base_tolerance_inside_circle
  expr: Constraints[18] = VarSet.Base_antenna_base_x
  expr: Constraints[19] = VarSet.Base_antenna_base_y
  sketch-geometry (9):
    g0: LineSegment [constr] StartX=-25 StartY=25 StartZ=0 EndX=-25 EndY=-25 EndZ=0
    g1: LineSegment [constr] StartX=-25 StartY=-25 StartZ=0 EndX=25 EndY=-25 EndZ=0
    g2: LineSegment [constr] StartX=25 StartY=-25 StartZ=0 EndX=25 EndY=25 EndZ=0
    g3: LineSegment [constr] StartX=25 StartY=25 StartZ=0 EndX=-25 EndY=25 EndZ=0
    g4: GeomPoint [constr] X=0 Y=0 Z=0
    g5: Circle CenterX=-25 CenterY=25 CenterZ=0 NormalX=0 NormalY=0 NormalZ=1 AngleXU=0 Radius=1.75
    g6: Circle CenterX=25 CenterY=25 CenterZ=0 NormalX=0 NormalY=0 NormalZ=1 AngleXU=0 Radius=1.75
    g7: Circle CenterX=25 CenterY=-25 CenterZ=0 NormalX=0 NormalY=0 NormalZ=1 AngleXU=0 Radius=1.75
    g8: Circle CenterX=-25 CenterY=-25 CenterZ=0 NormalX=0 NormalY=0 NormalZ=1 AngleXU=0 Radius=1.75
  constraints (20):
    c: Coincident(g0,g1)
    c: Coincident(g1,g2)
    c: Coincident(g2,g3)
    c: Coincident(g3,g0)
    c: Vertical(g0)
    c: Vertical(g2)
    c: Horizontal(g1)
    c: Horizontal(g3)
    c: Symmetric(g2,g0,g4)
    c: Coincident(g4,g-1)
    c: Coincident(g5,g0)
    c: Coincident(g6,g2)
    c: Coincident(g7,g1)
    c: Coincident(g8,g0)
    c: Equal(g5,g6)
    c: Equal(g6,g7)
    c: Equal(g7,g8)
    c: Diameter(g5) = 3.5
    c: DistanceX(g0,g2) = 50
    c: DistanceY(g0,g0) = 50
FEATURE [Sketcher::SketchObject] Sketch055  label="hex002"
  ArcFitTolerance = 1e-06
  AttachmentSupport = -> [XY_Plane034]
  ExternalGeometry = -> [Sketch054]
  ExternalTypes = [0]
  FullyConstrained = true
  MakeInternals = false
  MapMode = 5
  expr: Constraints[79] = 5.7 mm + VarSet.Base_tolerance_inside_circle
  sketch-geometry (28):
    g0: LineSegment StartX=-21.5359 StartY=25 StartZ=0 EndX=-23.2679 EndY=28 EndZ=0
    g1: LineSegment StartX=-23.2679 StartY=28 StartZ=0 EndX=-26.7321 EndY=28 EndZ=0
    g2: LineSegment StartX=-26.7321 StartY=28 StartZ=0 EndX=-28.4641 EndY=25 EndZ=0
    g3: LineSegment StartX=-28.4641 StartY=25 StartZ=0 EndX=-26.7321 EndY=22 EndZ=0
    g4: LineSegment StartX=-26.7321 StartY=22 StartZ=0 EndX=-23.2679 EndY=22 EndZ=0
    g5: LineSegment StartX=-23.2679 StartY=22 StartZ=0 EndX=-21.5359 EndY=25 EndZ=0
    g6: Circle [constr] CenterX=-25 CenterY=25 CenterZ=0 NormalX=0 NormalY=0 NormalZ=1 AngleXU=0 Radius=3.4641
    g7: LineSegment StartX=-23.2679 StartY=-22 StartZ=0 EndX=-26.7321 EndY=-22 EndZ=0
    g8: LineSegment StartX=-26.7321 StartY=-22 StartZ=0 EndX=-28.4641 EndY=-25 EndZ=0
    g9: LineSegment StartX=-28.4641 StartY=-25 StartZ=0 EndX=-26.7321 EndY=-28 EndZ=0
    g10: LineSegment StartX=-26.7321 StartY=-28 StartZ=0 EndX=-23.2679 EndY=-28 EndZ=0
    g11: LineSegment StartX=-23.2679 StartY=-28 StartZ=0 EndX=-21.5359 EndY=-25 EndZ=0
    g12: LineSegment StartX=-21.5359 StartY=-25 StartZ=0 EndX=-23.2679 EndY=-22 EndZ=0
    g13: Circle [constr] CenterX=-25 CenterY=-25 CenterZ=0 NormalX=0 NormalY=0 NormalZ=1 AngleXU=0 Radius=3.4641
    g14: LineSegment StartX=26.7321 StartY=22 StartZ=0 EndX=28.4641 EndY=25 EndZ=0
    g15: LineSegment StartX=28.4641 StartY=25 StartZ=0 EndX=26.7321 EndY=28 EndZ=0
    g16: LineSegment StartX=26.7321 StartY=28 StartZ=0 EndX=23.2679 EndY=28 EndZ=0
    g17: LineSegment StartX=23.2679 StartY=28 StartZ=0 EndX=21.5359 EndY=25 EndZ=0
    g18: LineSegment StartX=21.5359 StartY=25 StartZ=0 EndX=23.2679 EndY=22 EndZ=0
    g19: LineSegment StartX=23.2679 StartY=22 StartZ=0 EndX=26.7321 EndY=22 EndZ=0
    g20: Circle [constr] CenterX=25 CenterY=25 CenterZ=0 NormalX=0 NormalY=0 NormalZ=1 AngleXU=0 Radius=3.4641
    g21: LineSegment StartX=23.2679 StartY=-22 StartZ=0 EndX=21.5359 EndY=-25 EndZ=0
    g22: LineSegment StartX=21.5359 StartY=-25 StartZ=0 EndX=23.2679 EndY=-28 EndZ=0
    g23: LineSegment StartX=23.2679 StartY=-28 StartZ=0 EndX=26.7321 EndY=-28 EndZ=0
    g24: LineSegment StartX=26.7321 StartY=-28 StartZ=0 EndX=28.4641 EndY=-25 EndZ=0
    g25: LineSegment StartX=28.4641 StartY=-25 StartZ=0 EndX=26.7321 EndY=-22 EndZ=0
    g26: LineSegment StartX=26.7321 StartY=-22 StartZ=0 EndX=23.2679 EndY=-22 EndZ=0
    g27: Circle [constr] CenterX=25 CenterY=-25 CenterZ=0 NormalX=0 NormalY=0 NormalZ=1 AngleXU=0 Radius=3.4641
  constraints (64):
    c: Coincident(g0,g1)
    c: Coincident(g1,g2)
    c: Coincident(g2,g3)
    c: Coincident(g3,g4)
    c: Coincident(g4,g5)
    c: Coincident(g5,g0)
    c: Equal(g0, g1-g5) x5
    c: PointOnObject(g0,g6)
    c: PointOnObject(g1,g6)
    c: PointOnObject(g2,g6)
    c: PointOnObject(g3,g6)
    c: PointOnObject(g4,g6)
    c: PointOnObject(g5,g6)
    c: Coincident(g6,g-3)
    c: Coincident(g7,g8)
    c: Coincident(g8,g9)
    c: Coincident(g9,g10)
    c: Coincident(g10,g11)
    c: Coincident(g11,g12)
    c: Coincident(g12,g7)
    c: Equal(g7, g8-g12) x5
    c: PointOnObject(g7,g13)
    c: PointOnObject(g8,g13)
    c: PointOnObject(g9,g13)
    c: PointOnObject(g10,g13)
    c: PointOnObject(g11,g13)
    c: PointOnObject(g12,g13)
    c: Coincident(g13,g-4)
    c: Coincident(g14,g15)
    c: Coincident(g15,g16)
    c: Coincident(g16,g17)
    c: Coincident(g17,g18)
    c: Coincident(g18,g19)
    c: Coincident(g19,g14)
    c: Equal(g14, g15-g19) x5
    c: PointOnObject(g14,g20)
    c: PointOnObject(g15,g20)
    c: PointOnObject(g16,g20)
    c: PointOnObject(g17,g20)
    c: PointOnObject(g18,g20)
    c: PointOnObject(g19,g20)
    c: Coincident(g20,g-6)
    c: Coincident(g21,g22)
    c: Coincident(g22,g23)
    c: Coincident(g23,g24)
    c: Coincident(g24,g25)
    c: Coincident(g25,g26)
    c: Coincident(g26,g21)
    c: Equal(g21, g22-g26) x5
    c: PointOnObject(g21,g27)
    c: PointOnObject(g22,g27)
    c: PointOnObject(g23,g27)
    c: PointOnObject(g24,g27)
    c: PointOnObject(g25,g27)
    c: PointOnObject(g26,g27)
    c: Coincident(g27,g-5)
    c: Parallel(g4,g-1)
    c: Parallel(g7,g-1)
    c: Parallel(g-1,g19)
    c: Parallel(g-1,g26)
    c: Equal(g6,g20)
    c: Equal(g20,g27)
    c: Equal(g27,g13)
    c: Distance(g1,g0) = 6
FEATURE [Sketcher::SketchObject] Sketch056  label="cover_hole"
  ArcFitTolerance = 1e-06
  AttachmentSupport = -> [XY_Plane034]
  ExternalTypes = [0]
  FullyConstrained = true
  MakeInternals = false
  MapMode = 5
  expr: Constraints[1] = VarSet.Base_m3_insert
  expr: Constraints[2] = VarSet.Base_bearing_cap_outside_diameter_hole
  sketch-geometry (1):
    g0: Circle CenterX=0 CenterY=26.4 CenterZ=0 NormalX=0 NormalY=0 NormalZ=1 AngleXU=0 Radius=2.1
  constraints (3):
    c: PointOnObject(g0,g-2)
    c: Diameter(g0) = 4.2
    c: DistanceY(g-1,g0) = 26.4
FEATURE [PartDesign::FeaturePython] InvoluteGear009  # WARN: FeaturePython — macro-defined, semantics opaque (R4)
  AttacherType = Attacher::AttachEngine3D
  Suppressed = false
  addendum_diameter = 95
  angular_backlash = 0
  axle_hole = false
  axle_holesize = 10
  backlash = 0
  clearance = 0.25
  double_helix = true
  head = 0
  head_fillet = 0
  height = 12
  helix_angle = 25
  module = 2.5
  num_teeth = 36
  numpoints = 20
  offset_hole = false
  offset_holeoffset = 10
  offset_holesize = 10
  pitch_diameter = 90
  pressure_angle = 20
  properties_from_tool = false
  reversed_backlash = false
  root_diameter = 83.75
  root_fillet = 0
  shift = 0
  simple = false
  transverse_pitch = 7.85398
  traverse_module = 2.5
  undercut = false
  version = 1.3.0
  expr: angular_backlash = backlash / pitch_diameter * 360 ° / pi
  expr: height = VarSet.Base_gear_thickness
FEATURE [PartDesign::Pocket] Pocket032
  BaseFeature = -> InvoluteGear009
  Direction = (0,0,-1)
  Length = 5
  Length2 = 5
  Midplane = true
  Profile = -> Sketch053 [Edge2]
  ReferenceAxis = -> Sketch053 [N_Axis]
  Refine = true
  Suppressed = false
  Type = 1
FEATURE [PartDesign::Pocket] Pocket033
  BaseFeature = -> Pocket032
  Direction = (0,0,-1)
  Length = 6.8
  Length2 = 5
  Profile = -> Sketch053 [Edge1]
  ReferenceAxis = -> Sketch053 [N_Axis]
  Refine = true
  Reversed = true
  Suppressed = false
  Type = 0
  expr: Length = VarSet.Base_bearing_thickness + VarSet.Base_base_bearing_cap_thickness
FEATURE [PartDesign::Pocket] Pocket034
  BaseFeature = -> Pocket033
  Direction = (0,0,-1)
  Length = 2
  Length2 = 5
  Profile = -> Sketch053 [Edge3]
  ReferenceAxis = -> Sketch053 [N_Axis]
  Refine = true
  Reversed = true
  Suppressed = false
  Type = 0
  expr: Length = VarSet.Base_base_bearing_cap_thickness
FEATURE [PartDesign::Pocket] Pocket035
  BaseFeature = -> Pocket034
  Direction = (0,0,-1)
  Length = 2.5
  Length2 = 5
  Profile = -> Sketch055
  ReferenceAxis = -> Sketch055 [N_Axis]
  Refine = true
  Reversed = true
  Suppressed = false
  Type = 0
FEATURE [PartDesign::Pocket] Pocket036
  BaseFeature = -> Pocket035
  Direction = (0,0,-1)
  Length = 5
  Length2 = 5
  Midplane = true
  Profile = -> Sketch054
  ReferenceAxis = -> Sketch054 [N_Axis]
  Refine = true
  Suppressed = false
  Type = 1
FEATURE [PartDesign::Pocket] Pocket037
  BaseFeature = -> Pocket036
  Direction = (0,0,-1)
  Length = 5
  Length2 = 5
  Midplane = true
  Profile = -> Sketch056
  ReferenceAxis = -> Sketch056 [N_Axis]
  Refine = true
  Suppressed = false
  Type = 1
FEATURE [PartDesign::PolarPattern] PolarPattern003
  Angle = 360
  Axis = -> Sketch056 [N_Axis]
  BaseFeature = -> Pocket037
  Mode = 0
  Occurrences = 4
  Offset = 120
  Originals = -> [Pocket037]
  Refine = true
  Suppressed = false
  TransformMode = 0
FEATURE [PartDesign::Body] Body018  label="wheel_el003"
  AllowCompound = false
  Group = -> [Sketch053,Sketch054,Sketch055,Sketch056,InvoluteGear009,Pocket032,Pocket033,Pocket034,Pocket035,Pocket036,Pocket037,PolarPattern003]
  Origin = -> Origin061
  Tip = -> PolarPattern003
PROVENANCE & LICENSES
A FreeCAD (.FCStd) document from a public repository crawl; recipes are the document's own serialized feature recipes (and, for linked parts, companion documents' recipes).
License: mit.
